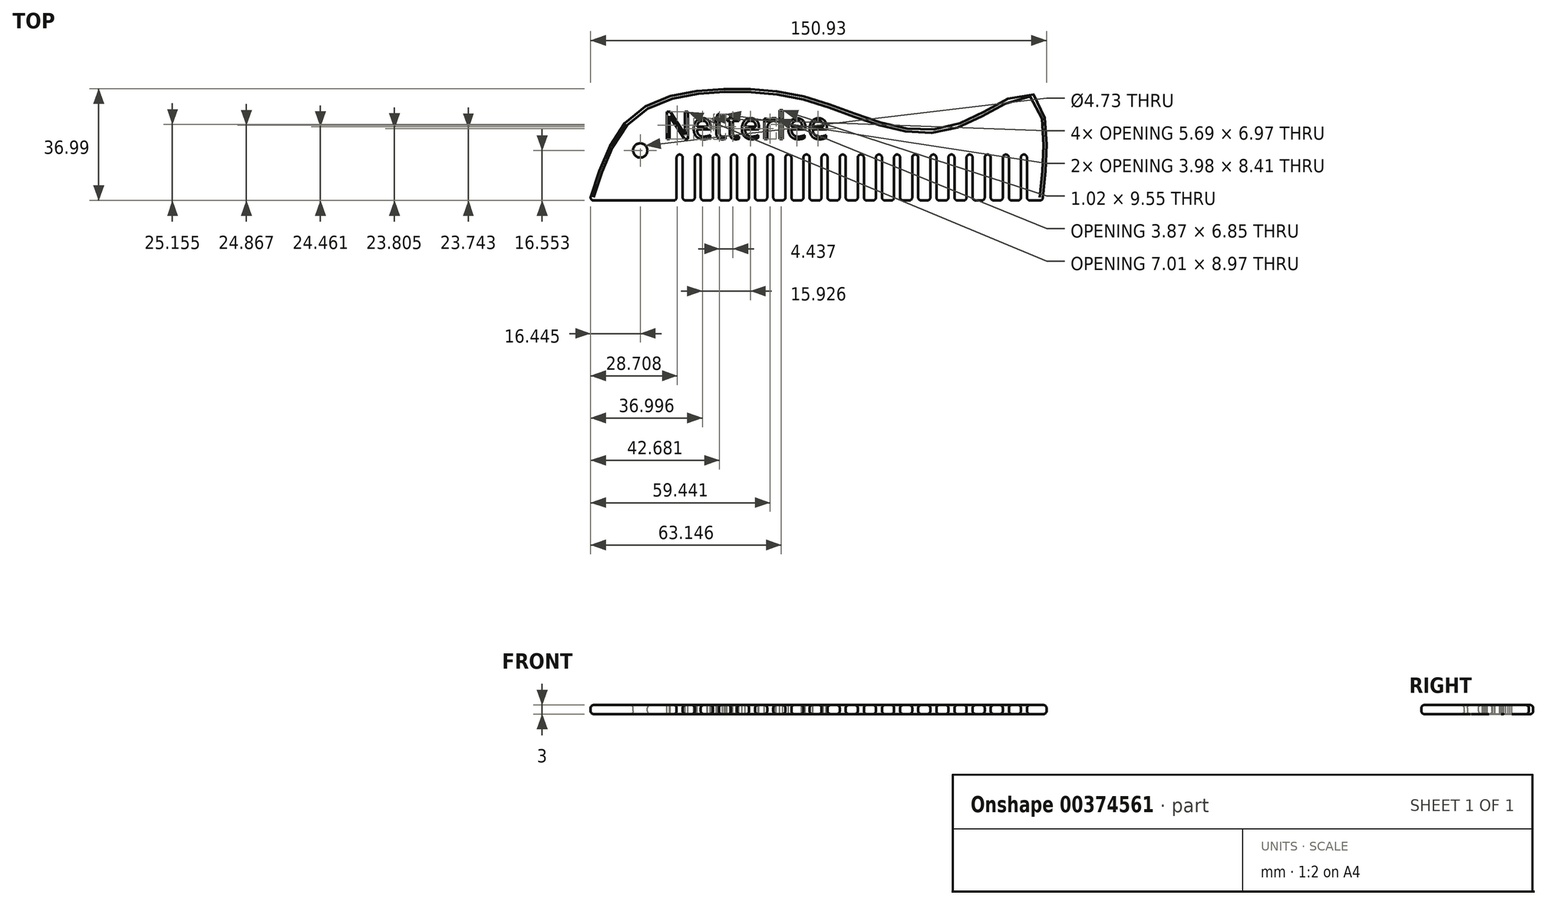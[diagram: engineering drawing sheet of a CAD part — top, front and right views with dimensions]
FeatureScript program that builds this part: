
annotation { "Feature Type Name" : "Feature", "Feature Type Description" : "" }
export const myFeature = defineFeature(function(context is Context, id is Id, definition is map)
    precondition{}
    {
        {
            var Q0;
            Q0=qCreatedBy(makeId("Top.planeOp"),FACE);
            var sketch = newSketch(context, id + "F0", { "sketchPlane" : qUnion([Q0])});
            skFitSpline(sketch, "E0", {"points": [v(-85.57, 36.82) * mm, v(-71.04, 65.23) * mm, v(-42.5, 73.69) * mm, v(-14.03, 71.1) * mm, v(9.11, 63.18) * mm, v(36.67, 62.2) * mm, v(61.65, 71.82) * mm, v(64.09, 33.9) * mm], "startDerivative": vector(69.4, 223.94) * mm, "endDerivative": vector(-31.57, -256.3) * mm});
            skLineSegment(sketch, "E1", {"start": v(-85.57, 36.82) * mm, "end": v(64.43, 36.82) * mm});
            skSolve(sketch);
        }
        {
            var Q0;
            {var subQ0=sQuery(id+"F0.wireOp",EDGE,"E1");Q0=makeQuery(id+"F0.imprint","IMPRINT",FACE,{"disambiguationData":[TD([[makeQuery(id+"F0.imprint","IMPRINT",EDGE,{"derivedFrom":subQ0}),1.0]])]});}
            extrude(context, id + "F1", {"entities" : qUnion([Q0]), "depth" : 3 * mm});
        }
        {
            var Q0;
            Q0=makeQuery(id+"F1.opExtrude","CAP_FACE",FACE,{"disambiguationData":[OSD([sQuery(id+"F0.wireOp",EDGE,"E0"),sQuery(id+"F0.wireOp",EDGE,"E1")])],"isStart":false});
            var sketch = newSketch(context, id + "F2", { "sketchPlane" : qUnion([Q0])});
            skLineSegment(sketch, "E2.bottom", {"start": v(-56.74, 52.03) * mm, "end": v(-54.74, 52.03) * mm});
            skLineSegment(sketch, "E2.top", {"start": v(-56.74, 30.03) * mm, "end": v(-54.74, 30.03) * mm});
            skLineSegment(sketch, "E2.left", {"start": v(-56.74, 52.03) * mm, "end": v(-56.74, 30.03) * mm});
            skLineSegment(sketch, "E2.right", {"start": v(-54.74, 52.03) * mm, "end": v(-54.74, 30.03) * mm});
            skLineSegment(sketch, "E3.1.0.0", {"start": v(-50.74, 52.03) * mm, "end": v(-50.74, 30.03) * mm});
            skLineSegment(sketch, "E3.1.0.1", {"start": v(-50.74, 52.03) * mm, "end": v(-48.74, 52.03) * mm});
            skLineSegment(sketch, "E3.1.0.2", {"start": v(-48.74, 52.03) * mm, "end": v(-48.74, 30.03) * mm});
            skLineSegment(sketch, "E3.1.0.3", {"start": v(-50.74, 30.03) * mm, "end": v(-48.74, 30.03) * mm});
            skLineSegment(sketch, "E3.2.0.0", {"start": v(-44.74, 52.03) * mm, "end": v(-44.74, 30.03) * mm});
            skLineSegment(sketch, "E3.2.0.1", {"start": v(-44.74, 52.03) * mm, "end": v(-42.74, 52.03) * mm});
            skLineSegment(sketch, "E3.2.0.2", {"start": v(-42.74, 52.03) * mm, "end": v(-42.74, 30.03) * mm});
            skLineSegment(sketch, "E3.2.0.3", {"start": v(-44.74, 30.03) * mm, "end": v(-42.74, 30.03) * mm});
            skLineSegment(sketch, "E3.3.0.0", {"start": v(-38.74, 52.03) * mm, "end": v(-38.74, 30.03) * mm});
            skLineSegment(sketch, "E3.3.0.1", {"start": v(-38.74, 52.03) * mm, "end": v(-36.74, 52.03) * mm});
            skLineSegment(sketch, "E3.3.0.2", {"start": v(-36.74, 52.03) * mm, "end": v(-36.74, 30.03) * mm});
            skLineSegment(sketch, "E3.3.0.3", {"start": v(-38.74, 30.03) * mm, "end": v(-36.74, 30.03) * mm});
            skLineSegment(sketch, "E3.4.0.0", {"start": v(-32.74, 52.03) * mm, "end": v(-32.74, 30.03) * mm});
            skLineSegment(sketch, "E3.4.0.1", {"start": v(-32.74, 52.03) * mm, "end": v(-30.74, 52.03) * mm});
            skLineSegment(sketch, "E3.4.0.2", {"start": v(-30.74, 52.03) * mm, "end": v(-30.74, 30.03) * mm});
            skLineSegment(sketch, "E3.4.0.3", {"start": v(-32.74, 30.03) * mm, "end": v(-30.74, 30.03) * mm});
            skLineSegment(sketch, "E3.5.0.0", {"start": v(-26.74, 52.03) * mm, "end": v(-26.74, 30.03) * mm});
            skLineSegment(sketch, "E3.5.0.1", {"start": v(-26.74, 52.03) * mm, "end": v(-24.74, 52.03) * mm});
            skLineSegment(sketch, "E3.5.0.2", {"start": v(-24.74, 52.03) * mm, "end": v(-24.74, 30.03) * mm});
            skLineSegment(sketch, "E3.5.0.3", {"start": v(-26.74, 30.03) * mm, "end": v(-24.74, 30.03) * mm});
            skLineSegment(sketch, "E3.6.0.0", {"start": v(-20.74, 52.03) * mm, "end": v(-20.74, 30.03) * mm});
            skLineSegment(sketch, "E3.6.0.1", {"start": v(-20.74, 52.03) * mm, "end": v(-18.74, 52.03) * mm});
            skLineSegment(sketch, "E3.6.0.2", {"start": v(-18.74, 52.03) * mm, "end": v(-18.74, 30.03) * mm});
            skLineSegment(sketch, "E3.6.0.3", {"start": v(-20.74, 30.03) * mm, "end": v(-18.74, 30.03) * mm});
            skLineSegment(sketch, "E3.7.0.0", {"start": v(-14.74, 52.03) * mm, "end": v(-14.74, 30.03) * mm});
            skLineSegment(sketch, "E3.7.0.1", {"start": v(-14.74, 52.03) * mm, "end": v(-12.74, 52.03) * mm});
            skLineSegment(sketch, "E3.7.0.2", {"start": v(-12.74, 52.03) * mm, "end": v(-12.74, 30.03) * mm});
            skLineSegment(sketch, "E3.7.0.3", {"start": v(-14.74, 30.03) * mm, "end": v(-12.74, 30.03) * mm});
            skLineSegment(sketch, "E3.8.0.0", {"start": v(-8.74, 52.03) * mm, "end": v(-8.74, 30.03) * mm});
            skLineSegment(sketch, "E3.8.0.1", {"start": v(-8.74, 52.03) * mm, "end": v(-6.74, 52.03) * mm});
            skLineSegment(sketch, "E3.8.0.2", {"start": v(-6.74, 52.03) * mm, "end": v(-6.74, 30.03) * mm});
            skLineSegment(sketch, "E3.8.0.3", {"start": v(-8.74, 30.03) * mm, "end": v(-6.74, 30.03) * mm});
            skLineSegment(sketch, "E3.9.0.0", {"start": v(-2.74, 52.03) * mm, "end": v(-2.74, 30.03) * mm});
            skLineSegment(sketch, "E3.9.0.1", {"start": v(-2.74, 52.03) * mm, "end": v(-0.74, 52.03) * mm});
            skLineSegment(sketch, "E3.9.0.2", {"start": v(-0.74, 52.03) * mm, "end": v(-0.74, 30.03) * mm});
            skLineSegment(sketch, "E3.9.0.3", {"start": v(-2.74, 30.03) * mm, "end": v(-0.74, 30.03) * mm});
            skLineSegment(sketch, "E3.10.0.0", {"start": v(3.26, 52.03) * mm, "end": v(3.26, 30.03) * mm});
            skLineSegment(sketch, "E3.10.0.1", {"start": v(3.26, 52.03) * mm, "end": v(5.26, 52.03) * mm});
            skLineSegment(sketch, "E3.10.0.2", {"start": v(5.26, 52.03) * mm, "end": v(5.26, 30.03) * mm});
            skLineSegment(sketch, "E3.10.0.3", {"start": v(3.26, 30.03) * mm, "end": v(5.26, 30.03) * mm});
            skLineSegment(sketch, "E3.11.0.0", {"start": v(9.26, 52.03) * mm, "end": v(9.26, 30.03) * mm});
            skLineSegment(sketch, "E3.11.0.1", {"start": v(9.26, 52.03) * mm, "end": v(11.26, 52.03) * mm});
            skLineSegment(sketch, "E3.11.0.2", {"start": v(11.26, 52.03) * mm, "end": v(11.26, 30.03) * mm});
            skLineSegment(sketch, "E3.11.0.3", {"start": v(9.26, 30.03) * mm, "end": v(11.26, 30.03) * mm});
            skLineSegment(sketch, "E3.12.0.0", {"start": v(15.26, 52.03) * mm, "end": v(15.26, 30.03) * mm});
            skLineSegment(sketch, "E3.12.0.1", {"start": v(15.26, 52.03) * mm, "end": v(17.26, 52.03) * mm});
            skLineSegment(sketch, "E3.12.0.2", {"start": v(17.26, 52.03) * mm, "end": v(17.26, 30.03) * mm});
            skLineSegment(sketch, "E3.12.0.3", {"start": v(15.26, 30.03) * mm, "end": v(17.26, 30.03) * mm});
            skLineSegment(sketch, "E3.13.0.0", {"start": v(21.26, 52.03) * mm, "end": v(21.26, 30.03) * mm});
            skLineSegment(sketch, "E3.13.0.1", {"start": v(21.26, 52.03) * mm, "end": v(23.26, 52.03) * mm});
            skLineSegment(sketch, "E3.13.0.2", {"start": v(23.26, 52.03) * mm, "end": v(23.26, 30.03) * mm});
            skLineSegment(sketch, "E3.13.0.3", {"start": v(21.26, 30.03) * mm, "end": v(23.26, 30.03) * mm});
            skLineSegment(sketch, "E3.14.0.0", {"start": v(27.26, 52.03) * mm, "end": v(27.26, 30.03) * mm});
            skLineSegment(sketch, "E3.14.0.1", {"start": v(27.26, 52.03) * mm, "end": v(29.26, 52.03) * mm});
            skLineSegment(sketch, "E3.14.0.2", {"start": v(29.26, 52.03) * mm, "end": v(29.26, 30.03) * mm});
            skLineSegment(sketch, "E3.14.0.3", {"start": v(27.26, 30.03) * mm, "end": v(29.26, 30.03) * mm});
            skLineSegment(sketch, "E3.direction1", {"start": v(-54.74, 30.03) * mm, "end": v(-48.74, 30.03) * mm, "construction": true});
            skLineSegment(sketch, "E4.0.15.0", {"start": v(33.26, 52.03) * mm, "end": v(33.26, 30.03) * mm});
            skLineSegment(sketch, "E4.3.15.0", {"start": v(33.26, 52.03) * mm, "end": v(35.26, 52.03) * mm});
            skLineSegment(sketch, "E4.6.15.0", {"start": v(35.26, 52.03) * mm, "end": v(35.26, 30.03) * mm});
            skLineSegment(sketch, "E4.9.15.0", {"start": v(33.26, 30.03) * mm, "end": v(35.26, 30.03) * mm});
            skLineSegment(sketch, "E4.0.16.0", {"start": v(39.26, 52.03) * mm, "end": v(39.26, 30.03) * mm});
            skLineSegment(sketch, "E4.3.16.0", {"start": v(39.26, 52.03) * mm, "end": v(41.26, 52.03) * mm});
            skLineSegment(sketch, "E4.6.16.0", {"start": v(41.26, 52.03) * mm, "end": v(41.26, 30.03) * mm});
            skLineSegment(sketch, "E4.9.16.0", {"start": v(39.26, 30.03) * mm, "end": v(41.26, 30.03) * mm});
            skLineSegment(sketch, "E4.0.17.0", {"start": v(45.26, 52.03) * mm, "end": v(45.26, 30.03) * mm});
            skLineSegment(sketch, "E4.3.17.0", {"start": v(45.26, 52.03) * mm, "end": v(47.26, 52.03) * mm});
            skLineSegment(sketch, "E4.6.17.0", {"start": v(47.26, 52.03) * mm, "end": v(47.26, 30.03) * mm});
            skLineSegment(sketch, "E4.9.17.0", {"start": v(45.26, 30.03) * mm, "end": v(47.26, 30.03) * mm});
            skLineSegment(sketch, "E5.0.18.0", {"start": v(51.26, 52.03) * mm, "end": v(51.26, 30.03) * mm});
            skLineSegment(sketch, "E5.3.18.0", {"start": v(51.26, 52.03) * mm, "end": v(53.26, 52.03) * mm});
            skLineSegment(sketch, "E5.6.18.0", {"start": v(53.26, 52.03) * mm, "end": v(53.26, 30.03) * mm});
            skLineSegment(sketch, "E5.9.18.0", {"start": v(51.26, 30.03) * mm, "end": v(53.26, 30.03) * mm});
            skLineSegment(sketch, "E5.0.19.0", {"start": v(57.26, 52.03) * mm, "end": v(57.26, 30.03) * mm});
            skLineSegment(sketch, "E5.3.19.0", {"start": v(57.26, 52.03) * mm, "end": v(59.26, 52.03) * mm});
            skLineSegment(sketch, "E5.6.19.0", {"start": v(59.26, 52.03) * mm, "end": v(59.26, 30.03) * mm});
            skLineSegment(sketch, "E5.9.19.0", {"start": v(57.26, 30.03) * mm, "end": v(59.26, 30.03) * mm});
            skCircle(sketch, "E6", {"center": v(-70.33, 52.78) * mm, "radius": 2.54 * mm});
            skSolve(sketch);
        }
        {
            var Q0;
            {var subQ0=sQuery(id+"F2.wireOp",EDGE,"E2.bottom");Q0=makeQuery(id+"F2.imprint","IMPRINT",FACE,{"disambiguationData":[TD([[makeQuery(id+"F2.imprint","IMPRINT",EDGE,{"derivedFrom":subQ0}),-1.0]])]});}
            var Q1;
            {var subQ0=sQuery(id+"F2.wireOp",EDGE,"E3.1.0.1");Q1=makeQuery(id+"F2.imprint","IMPRINT",FACE,{"disambiguationData":[TD([[makeQuery(id+"F2.imprint","IMPRINT",EDGE,{"derivedFrom":subQ0}),-1.0]])]});}
            var Q2;
            {var subQ0=sQuery(id+"F2.wireOp",EDGE,"E3.2.0.1");Q2=makeQuery(id+"F2.imprint","IMPRINT",FACE,{"disambiguationData":[TD([[makeQuery(id+"F2.imprint","IMPRINT",EDGE,{"derivedFrom":subQ0}),-1.0]])]});}
            var Q3;
            {var subQ0=sQuery(id+"F2.wireOp",EDGE,"E3.3.0.1");Q3=makeQuery(id+"F2.imprint","IMPRINT",FACE,{"disambiguationData":[TD([[makeQuery(id+"F2.imprint","IMPRINT",EDGE,{"derivedFrom":subQ0}),-1.0]])]});}
            var Q4;
            {var subQ0=sQuery(id+"F2.wireOp",EDGE,"E3.4.0.1");Q4=makeQuery(id+"F2.imprint","IMPRINT",FACE,{"disambiguationData":[TD([[makeQuery(id+"F2.imprint","IMPRINT",EDGE,{"derivedFrom":subQ0}),-1.0]])]});}
            var Q5;
            {var subQ0=sQuery(id+"F2.wireOp",EDGE,"E3.5.0.1");Q5=makeQuery(id+"F2.imprint","IMPRINT",FACE,{"disambiguationData":[TD([[makeQuery(id+"F2.imprint","IMPRINT",EDGE,{"derivedFrom":subQ0}),-1.0]])]});}
            var Q6;
            {var subQ0=sQuery(id+"F2.wireOp",EDGE,"E3.6.0.1");Q6=makeQuery(id+"F2.imprint","IMPRINT",FACE,{"disambiguationData":[TD([[makeQuery(id+"F2.imprint","IMPRINT",EDGE,{"derivedFrom":subQ0}),-1.0]])]});}
            var Q7;
            {var subQ0=sQuery(id+"F2.wireOp",EDGE,"E3.7.0.1");Q7=makeQuery(id+"F2.imprint","IMPRINT",FACE,{"disambiguationData":[TD([[makeQuery(id+"F2.imprint","IMPRINT",EDGE,{"derivedFrom":subQ0}),-1.0]])]});}
            var Q8;
            {var subQ0=sQuery(id+"F2.wireOp",EDGE,"E3.8.0.1");Q8=makeQuery(id+"F2.imprint","IMPRINT",FACE,{"disambiguationData":[TD([[makeQuery(id+"F2.imprint","IMPRINT",EDGE,{"derivedFrom":subQ0}),-1.0]])]});}
            var Q9;
            {var subQ0=sQuery(id+"F2.wireOp",EDGE,"E3.9.0.1");Q9=makeQuery(id+"F2.imprint","IMPRINT",FACE,{"disambiguationData":[TD([[makeQuery(id+"F2.imprint","IMPRINT",EDGE,{"derivedFrom":subQ0}),-1.0]])]});}
            var Q10;
            {var subQ0=sQuery(id+"F2.wireOp",EDGE,"E3.10.0.1");Q10=makeQuery(id+"F2.imprint","IMPRINT",FACE,{"disambiguationData":[TD([[makeQuery(id+"F2.imprint","IMPRINT",EDGE,{"derivedFrom":subQ0}),-1.0]])]});}
            var Q11;
            {var subQ0=sQuery(id+"F2.wireOp",EDGE,"E3.11.0.1");Q11=makeQuery(id+"F2.imprint","IMPRINT",FACE,{"disambiguationData":[TD([[makeQuery(id+"F2.imprint","IMPRINT",EDGE,{"derivedFrom":subQ0}),-1.0]])]});}
            var Q12;
            {var subQ0=sQuery(id+"F2.wireOp",EDGE,"E3.12.0.1");Q12=makeQuery(id+"F2.imprint","IMPRINT",FACE,{"disambiguationData":[TD([[makeQuery(id+"F2.imprint","IMPRINT",EDGE,{"derivedFrom":subQ0}),-1.0]])]});}
            var Q13;
            {var subQ0=sQuery(id+"F2.wireOp",EDGE,"E3.13.0.1");Q13=makeQuery(id+"F2.imprint","IMPRINT",FACE,{"disambiguationData":[TD([[makeQuery(id+"F2.imprint","IMPRINT",EDGE,{"derivedFrom":subQ0}),-1.0]])]});}
            var Q14;
            {var subQ0=sQuery(id+"F2.wireOp",EDGE,"E3.14.0.1");Q14=makeQuery(id+"F2.imprint","IMPRINT",FACE,{"disambiguationData":[TD([[makeQuery(id+"F2.imprint","IMPRINT",EDGE,{"derivedFrom":subQ0}),-1.0]])]});}
            var Q15;
            {var subQ0=sQuery(id+"F2.wireOp",EDGE,"E4.3.15.0");Q15=makeQuery(id+"F2.imprint","IMPRINT",FACE,{"disambiguationData":[TD([[makeQuery(id+"F2.imprint","IMPRINT",EDGE,{"derivedFrom":subQ0}),-1.0]])]});}
            var Q16;
            {var subQ0=sQuery(id+"F2.wireOp",EDGE,"E4.3.16.0");Q16=makeQuery(id+"F2.imprint","IMPRINT",FACE,{"disambiguationData":[TD([[makeQuery(id+"F2.imprint","IMPRINT",EDGE,{"derivedFrom":subQ0}),-1.0]])]});}
            var Q17;
            {var subQ0=sQuery(id+"F2.wireOp",EDGE,"E4.3.17.0");Q17=makeQuery(id+"F2.imprint","IMPRINT",FACE,{"disambiguationData":[TD([[makeQuery(id+"F2.imprint","IMPRINT",EDGE,{"derivedFrom":subQ0}),-1.0]])]});}
            var Q18;
            {var subQ0=sQuery(id+"F2.wireOp",EDGE,"E5.3.18.0");Q18=makeQuery(id+"F2.imprint","IMPRINT",FACE,{"disambiguationData":[TD([[makeQuery(id+"F2.imprint","IMPRINT",EDGE,{"derivedFrom":subQ0}),-1.0]])]});}
            var Q19;
            {var subQ0=sQuery(id+"F2.wireOp",EDGE,"E5.3.19.0");Q19=makeQuery(id+"F2.imprint","IMPRINT",FACE,{"disambiguationData":[TD([[makeQuery(id+"F2.imprint","IMPRINT",EDGE,{"derivedFrom":subQ0}),-1.0]])]});}
            extrude(context, id + "F3", {"entities" : qUnion([Q0, Q1, Q2, Q3, Q4, Q5, Q6, Q7, Q8, Q9, Q10, Q11, Q12, Q13, Q14, Q15, Q16, Q17, Q18, Q19]), "operationType" : NewBodyOperationType.REMOVE, "oppositeDirection" : true, "depth" : 5 * mm});
        }
        {
            var Q0;
            Q0=makeQuery(id+"F3.boolean.opBoolean","COPY",FACE,{"derivedFrom":makeQuery(id+"F3.opExtrude","SWEPT_FACE",FACE,{"disambiguationData":[OSD([sQuery(id+"F2.wireOp",EDGE,"E3.5.0.0")])]})});
            var Q1;
            Q1=makeQuery(id+"F1.opExtrude","CAP_EDGE",EDGE,{"disambiguationData":[OSD([sQuery(id+"F0.wireOp",EDGE,"E0")])],"isStart":false});
            var Q2;
            Q2=makeQuery(id+"F1.opExtrude","CAP_EDGE",EDGE,{"disambiguationData":[OSD([sQuery(id+"F0.wireOp",EDGE,"E0")])],"isStart":true});
            var Q3;
            Q3=makeQuery(id+"F1.opExtrude","SWEPT_FACE",FACE,{"disambiguationData":[OSD([sQuery(id+"F0.wireOp",EDGE,"E0")])]});
            var Q4;
            Q4=makeQuery(id+"F3.boolean.opBoolean","COPY",FACE,{"derivedFrom":makeQuery(id+"F3.opExtrude","SWEPT_FACE",FACE,{"disambiguationData":[OSD([sQuery(id+"F2.wireOp",EDGE,"E3.4.0.2")])]})});
            var Q5;
            Q5=makeQuery(id+"F3.boolean.opBoolean","COPY",FACE,{"derivedFrom":makeQuery(id+"F3.opExtrude","SWEPT_FACE",FACE,{"disambiguationData":[OSD([sQuery(id+"F2.wireOp",EDGE,"E2.left")])]})});
            var Q6;
            Q6=makeQuery(id+"F3.boolean.opBoolean","COPY",FACE,{"derivedFrom":makeQuery(id+"F3.opExtrude","SWEPT_FACE",FACE,{"disambiguationData":[OSD([sQuery(id+"F2.wireOp",EDGE,"E2.right")])]})});
            var Q7;
            Q7=makeQuery(id+"F3.boolean.opBoolean","COPY",FACE,{"derivedFrom":makeQuery(id+"F3.opExtrude","SWEPT_FACE",FACE,{"disambiguationData":[OSD([sQuery(id+"F2.wireOp",EDGE,"E3.1.0.0")])]})});
            var Q8;
            Q8=makeQuery(id+"F3.boolean.opBoolean","COPY",FACE,{"derivedFrom":makeQuery(id+"F3.opExtrude","SWEPT_FACE",FACE,{"disambiguationData":[OSD([sQuery(id+"F2.wireOp",EDGE,"E3.1.0.2")])]})});
            var Q9;
            Q9=makeQuery(id+"F3.boolean.opBoolean","COPY",FACE,{"derivedFrom":makeQuery(id+"F3.opExtrude","SWEPT_FACE",FACE,{"disambiguationData":[OSD([sQuery(id+"F2.wireOp",EDGE,"E3.2.0.0")])]})});
            var Q10;
            Q10=makeQuery(id+"F3.boolean.opBoolean","COPY",FACE,{"derivedFrom":makeQuery(id+"F3.opExtrude","SWEPT_FACE",FACE,{"disambiguationData":[OSD([sQuery(id+"F2.wireOp",EDGE,"E3.2.0.2")])]})});
            var Q11;
            Q11=makeQuery(id+"F3.boolean.opBoolean","COPY",FACE,{"derivedFrom":makeQuery(id+"F3.opExtrude","SWEPT_FACE",FACE,{"disambiguationData":[OSD([sQuery(id+"F2.wireOp",EDGE,"E3.3.0.0")])]})});
            var Q12;
            Q12=makeQuery(id+"F3.boolean.opBoolean","COPY",FACE,{"derivedFrom":makeQuery(id+"F3.opExtrude","SWEPT_FACE",FACE,{"disambiguationData":[OSD([sQuery(id+"F2.wireOp",EDGE,"E3.3.0.2")])]})});
            var Q13;
            Q13=makeQuery(id+"F3.boolean.opBoolean","COPY",FACE,{"derivedFrom":makeQuery(id+"F3.opExtrude","SWEPT_FACE",FACE,{"disambiguationData":[OSD([sQuery(id+"F2.wireOp",EDGE,"E3.4.0.0")])]})});
            var Q14;
            Q14=makeQuery(id+"F3.boolean.opBoolean","COPY",FACE,{"derivedFrom":makeQuery(id+"F3.opExtrude","SWEPT_FACE",FACE,{"disambiguationData":[OSD([sQuery(id+"F2.wireOp",EDGE,"E4.6.15.0")])]})});
            var Q15;
            {var subQ1=sQuery(id+"F0.wireOp",EDGE,"E1");Q15=makeQuery(id+"F3.boolean.opBoolean","SPLIT",FACE,{"disambiguationData":[TD([makeQuery(id+"F3.opExtrude","SWEPT_FACE",FACE,{"disambiguationData":[OSD([sQuery(id+"F2.wireOp",EDGE,"E5.6.19.0")])]})])],"derivedFrom":makeQuery(id+"F1.opExtrude","SWEPT_FACE",FACE,{"disambiguationData":[OSD([subQ1])]})});}
            var Q16;
            Q16=makeQuery(id+"F3.boolean.opBoolean","COPY",EDGE,{"derivedFrom":makeQuery(id+"F3.opExtrude","CAP_EDGE",EDGE,{"disambiguationData":[OSD([sQuery(id+"F2.wireOp",EDGE,"E3.9.0.2")])],"isStart":true})});
            var Q17;
            Q17=makeQuery(id+"F3.boolean.opBoolean","COPY",EDGE,{"derivedFrom":makeQuery(id+"F3.opExtrude","CAP_EDGE",EDGE,{"disambiguationData":[OSD([sQuery(id+"F2.wireOp",EDGE,"E4.0.15.0")])],"isStart":true})});
            var Q18;
            Q18=makeQuery(id+"F3.boolean.opBoolean","COPY",FACE,{"derivedFrom":makeQuery(id+"F3.opExtrude","SWEPT_FACE",FACE,{"disambiguationData":[OSD([sQuery(id+"F2.wireOp",EDGE,"E3.9.0.2")])]})});
            var Q19;
            Q19=makeQuery(id+"F3.boolean.opBoolean","COPY",FACE,{"derivedFrom":makeQuery(id+"F3.opExtrude","SWEPT_FACE",FACE,{"disambiguationData":[OSD([sQuery(id+"F2.wireOp",EDGE,"E4.0.15.0")])]})});
            var Q20;
            Q20=makeQuery(id+"F1.opExtrude","CAP_FACE",FACE,{"disambiguationData":[OSD([sQuery(id+"F0.wireOp",EDGE,"E0"),sQuery(id+"F0.wireOp",EDGE,"E1")])],"isStart":false});
            var Q21;
            Q21=makeQuery(id+"F3.boolean.opBoolean","COPY",EDGE,{"derivedFrom":makeQuery(id+"F3.opExtrude","CAP_EDGE",EDGE,{"disambiguationData":[OSD([sQuery(id+"F2.wireOp",EDGE,"E3.4.0.2")])],"isStart":true})});
            var Q22;
            Q22=makeQuery(id+"F3.boolean.opBoolean","COPY",EDGE,{"derivedFrom":makeQuery(id+"F3.opExtrude","CAP_EDGE",EDGE,{"disambiguationData":[OSD([sQuery(id+"F2.wireOp",EDGE,"E3.10.0.0")])],"isStart":true})});
            var Q23;
            Q23=makeQuery(id+"F3.boolean.opBoolean","COPY",FACE,{"derivedFrom":makeQuery(id+"F3.opExtrude","SWEPT_FACE",FACE,{"disambiguationData":[OSD([sQuery(id+"F2.wireOp",EDGE,"E3.10.0.0")])]})});
            var Q24;
            {var subQ1=sQuery(id+"F0.wireOp",EDGE,"E1");Q24=makeQuery(id+"F3.boolean.opBoolean","SPLIT",FACE,{"disambiguationData":[TD([makeQuery(id+"F3.opExtrude","SWEPT_FACE",FACE,{"disambiguationData":[OSD([sQuery(id+"F2.wireOp",EDGE,"E2.left")])]})])],"derivedFrom":makeQuery(id+"F1.opExtrude","SWEPT_FACE",FACE,{"disambiguationData":[OSD([subQ1])]})});}
            var Q25;
            Q25=makeQuery(id+"F3.boolean.opBoolean","COPY",EDGE,{"derivedFrom":makeQuery(id+"F3.opExtrude","CAP_EDGE",EDGE,{"disambiguationData":[OSD([sQuery(id+"F2.wireOp",EDGE,"E3.5.0.0")])],"isStart":true})});
            var Q26;
            Q26=makeQuery(id+"F3.boolean.opBoolean","COPY",EDGE,{"derivedFrom":makeQuery(id+"F3.opExtrude","CAP_EDGE",EDGE,{"disambiguationData":[OSD([sQuery(id+"F2.wireOp",EDGE,"E4.6.15.0")])],"isStart":true})});
            var Q27;
            Q27=makeQuery(id+"F3.boolean.opBoolean","COPY",EDGE,{"derivedFrom":makeQuery(id+"F3.opExtrude","CAP_EDGE",EDGE,{"disambiguationData":[OSD([sQuery(id+"F2.wireOp",EDGE,"E3.10.0.2")])],"isStart":true})});
            var Q28;
            Q28=makeQuery(id+"F3.boolean.opBoolean","COPY",EDGE,{"derivedFrom":makeQuery(id+"F3.opExtrude","CAP_EDGE",EDGE,{"disambiguationData":[OSD([sQuery(id+"F2.wireOp",EDGE,"E4.0.16.0")])],"isStart":true})});
            var Q29;
            Q29=makeQuery(id+"F3.boolean.opBoolean","COPY",FACE,{"derivedFrom":makeQuery(id+"F3.opExtrude","SWEPT_FACE",FACE,{"disambiguationData":[OSD([sQuery(id+"F2.wireOp",EDGE,"E3.10.0.2")])]})});
            var Q30;
            Q30=makeQuery(id+"F3.boolean.opBoolean","COPY",FACE,{"derivedFrom":makeQuery(id+"F3.opExtrude","SWEPT_FACE",FACE,{"disambiguationData":[OSD([sQuery(id+"F2.wireOp",EDGE,"E4.0.16.0")])]})});
            var Q31;
            Q31=makeQuery(id+"F3.boolean.opBoolean","COPY",EDGE,{"derivedFrom":makeQuery(id+"F3.opExtrude","CAP_EDGE",EDGE,{"disambiguationData":[OSD([sQuery(id+"F2.wireOp",EDGE,"E2.left")])],"isStart":true})});
            var Q32;
            Q32=makeQuery(id+"F3.boolean.opBoolean","COPY",EDGE,{"derivedFrom":makeQuery(id+"F3.opExtrude","CAP_EDGE",EDGE,{"disambiguationData":[OSD([sQuery(id+"F2.wireOp",EDGE,"E3.5.0.2")])],"isStart":true})});
            var Q33;
            Q33=makeQuery(id+"F3.boolean.opBoolean","COPY",EDGE,{"derivedFrom":makeQuery(id+"F3.opExtrude","CAP_EDGE",EDGE,{"disambiguationData":[OSD([sQuery(id+"F2.wireOp",EDGE,"E3.11.0.0")])],"isStart":true})});
            var Q34;
            Q34=makeQuery(id+"F3.boolean.opBoolean","COPY",FACE,{"derivedFrom":makeQuery(id+"F3.opExtrude","SWEPT_FACE",FACE,{"disambiguationData":[OSD([sQuery(id+"F2.wireOp",EDGE,"E3.5.0.2")])]})});
            var Q35;
            {var subQ0=sQuery(id+"F0.wireOp",EDGE,"E1");Q35=makeQuery(id+"F3.boolean.opBoolean","SPLIT",FACE,{"disambiguationData":[TD([makeQuery(id+"F3.opExtrude","SWEPT_FACE",FACE,{"disambiguationData":[OSD([sQuery(id+"F2.wireOp",EDGE,"E3.1.0.2")])]})])],"derivedFrom":makeQuery(id+"F1.opExtrude","SWEPT_FACE",FACE,{"disambiguationData":[OSD([subQ0])]})});}
            var Q36;
            Q36=makeQuery(id+"F3.boolean.opBoolean","COPY",EDGE,{"derivedFrom":makeQuery(id+"F3.opExtrude","CAP_EDGE",EDGE,{"disambiguationData":[OSD([sQuery(id+"F2.wireOp",EDGE,"E2.right")])],"isStart":true})});
            var Q37;
            Q37=makeQuery(id+"F3.boolean.opBoolean","COPY",FACE,{"derivedFrom":makeQuery(id+"F3.opExtrude","SWEPT_FACE",FACE,{"disambiguationData":[OSD([sQuery(id+"F2.wireOp",EDGE,"E3.6.0.0")])]})});
            var Q38;
            Q38=makeQuery(id+"F3.boolean.opBoolean","COPY",FACE,{"derivedFrom":makeQuery(id+"F3.opExtrude","SWEPT_FACE",FACE,{"disambiguationData":[OSD([sQuery(id+"F2.wireOp",EDGE,"E4.6.16.0")])]})});
            var Q39;
            Q39=makeQuery(id+"F3.boolean.opBoolean","COPY",EDGE,{"derivedFrom":makeQuery(id+"F3.opExtrude","CAP_EDGE",EDGE,{"disambiguationData":[OSD([sQuery(id+"F2.wireOp",EDGE,"E3.1.0.0")])],"isStart":true})});
            var Q40;
            Q40=makeQuery(id+"F3.boolean.opBoolean","COPY",EDGE,{"derivedFrom":makeQuery(id+"F3.opExtrude","CAP_EDGE",EDGE,{"disambiguationData":[OSD([sQuery(id+"F2.wireOp",EDGE,"E3.11.0.2")])],"isStart":true})});
            var Q41;
            Q41=makeQuery(id+"F3.boolean.opBoolean","COPY",EDGE,{"derivedFrom":makeQuery(id+"F3.opExtrude","CAP_EDGE",EDGE,{"disambiguationData":[OSD([sQuery(id+"F2.wireOp",EDGE,"E4.0.17.0")])],"isStart":true})});
            var Q42;
            Q42=makeQuery(id+"F3.boolean.opBoolean","COPY",FACE,{"derivedFrom":makeQuery(id+"F3.opExtrude","SWEPT_FACE",FACE,{"disambiguationData":[OSD([sQuery(id+"F2.wireOp",EDGE,"E3.11.0.2")])]})});
            var Q43;
            Q43=makeQuery(id+"F3.boolean.opBoolean","COPY",FACE,{"derivedFrom":makeQuery(id+"F3.opExtrude","SWEPT_FACE",FACE,{"disambiguationData":[OSD([sQuery(id+"F2.wireOp",EDGE,"E4.0.17.0")])]})});
            var Q44;
            Q44=makeQuery(id+"F3.boolean.opBoolean","COPY",EDGE,{"derivedFrom":makeQuery(id+"F3.opExtrude","CAP_EDGE",EDGE,{"disambiguationData":[OSD([sQuery(id+"F2.wireOp",EDGE,"E3.12.0.0")])],"isStart":true})});
            var Q45;
            Q45=makeQuery(id+"F3.boolean.opBoolean","COPY",FACE,{"derivedFrom":makeQuery(id+"F3.opExtrude","SWEPT_FACE",FACE,{"disambiguationData":[OSD([sQuery(id+"F2.wireOp",EDGE,"E3.6.0.2")])]})});
            var Q46;
            Q46=makeQuery(id+"F3.boolean.opBoolean","COPY",FACE,{"derivedFrom":makeQuery(id+"F3.opExtrude","SWEPT_FACE",FACE,{"disambiguationData":[OSD([sQuery(id+"F2.wireOp",EDGE,"E3.12.0.0")])]})});
            var Q47;
            Q47=makeQuery(id+"F3.boolean.opBoolean","COPY",EDGE,{"derivedFrom":makeQuery(id+"F3.opExtrude","CAP_EDGE",EDGE,{"disambiguationData":[OSD([sQuery(id+"F2.wireOp",EDGE,"E3.7.0.0")])],"isStart":true})});
            var Q48;
            Q48=makeQuery(id+"F3.boolean.opBoolean","COPY",EDGE,{"derivedFrom":makeQuery(id+"F3.opExtrude","CAP_EDGE",EDGE,{"disambiguationData":[OSD([sQuery(id+"F2.wireOp",EDGE,"E4.6.17.0")])],"isStart":true})});
            var Q49;
            Q49=makeQuery(id+"F3.boolean.opBoolean","COPY",FACE,{"derivedFrom":makeQuery(id+"F3.opExtrude","SWEPT_FACE",FACE,{"disambiguationData":[OSD([sQuery(id+"F2.wireOp",EDGE,"E3.7.0.0")])]})});
            var Q50;
            Q50=makeQuery(id+"F3.boolean.opBoolean","COPY",FACE,{"derivedFrom":makeQuery(id+"F3.opExtrude","SWEPT_FACE",FACE,{"disambiguationData":[OSD([sQuery(id+"F2.wireOp",EDGE,"E4.6.17.0")])]})});
            var Q51;
            Q51=makeQuery(id+"F3.boolean.opBoolean","COPY",EDGE,{"derivedFrom":makeQuery(id+"F3.opExtrude","CAP_EDGE",EDGE,{"disambiguationData":[OSD([sQuery(id+"F2.wireOp",EDGE,"E3.2.0.0")])],"isStart":true})});
            var Q52;
            Q52=makeQuery(id+"F3.boolean.opBoolean","COPY",EDGE,{"derivedFrom":makeQuery(id+"F3.opExtrude","CAP_EDGE",EDGE,{"disambiguationData":[OSD([sQuery(id+"F2.wireOp",EDGE,"E3.12.0.2")])],"isStart":true})});
            var Q53;
            Q53=makeQuery(id+"F3.boolean.opBoolean","COPY",EDGE,{"derivedFrom":makeQuery(id+"F3.opExtrude","CAP_EDGE",EDGE,{"disambiguationData":[OSD([sQuery(id+"F2.wireOp",EDGE,"E5.0.18.0")])],"isStart":true})});
            var Q54;
            Q54=makeQuery(id+"F3.boolean.opBoolean","COPY",FACE,{"derivedFrom":makeQuery(id+"F3.opExtrude","SWEPT_FACE",FACE,{"disambiguationData":[OSD([sQuery(id+"F2.wireOp",EDGE,"E3.12.0.2")])]})});
            var Q55;
            Q55=makeQuery(id+"F3.boolean.opBoolean","COPY",FACE,{"derivedFrom":makeQuery(id+"F3.opExtrude","SWEPT_FACE",FACE,{"disambiguationData":[OSD([sQuery(id+"F2.wireOp",EDGE,"E5.0.18.0")])]})});
            var Q56;
            Q56=makeQuery(id+"F3.boolean.opBoolean","COPY",EDGE,{"derivedFrom":makeQuery(id+"F3.opExtrude","CAP_EDGE",EDGE,{"disambiguationData":[OSD([sQuery(id+"F2.wireOp",EDGE,"E3.7.0.2")])],"isStart":true})});
            var Q57;
            Q57=makeQuery(id+"F3.boolean.opBoolean","COPY",EDGE,{"derivedFrom":makeQuery(id+"F3.opExtrude","CAP_EDGE",EDGE,{"disambiguationData":[OSD([sQuery(id+"F2.wireOp",EDGE,"E3.13.0.0")])],"isStart":true})});
            var Q58;
            Q58=makeQuery(id+"F3.boolean.opBoolean","COPY",FACE,{"derivedFrom":makeQuery(id+"F3.opExtrude","SWEPT_FACE",FACE,{"disambiguationData":[OSD([sQuery(id+"F2.wireOp",EDGE,"E3.7.0.2")])]})});
            var Q59;
            Q59=makeQuery(id+"F3.boolean.opBoolean","COPY",FACE,{"derivedFrom":makeQuery(id+"F3.opExtrude","SWEPT_FACE",FACE,{"disambiguationData":[OSD([sQuery(id+"F2.wireOp",EDGE,"E3.13.0.0")])]})});
            var Q60;
            Q60=makeQuery(id+"F3.boolean.opBoolean","COPY",EDGE,{"derivedFrom":makeQuery(id+"F3.opExtrude","CAP_EDGE",EDGE,{"disambiguationData":[OSD([sQuery(id+"F2.wireOp",EDGE,"E3.2.0.2")])],"isStart":true})});
            var Q61;
            Q61=makeQuery(id+"F3.boolean.opBoolean","COPY",EDGE,{"derivedFrom":makeQuery(id+"F3.opExtrude","CAP_EDGE",EDGE,{"disambiguationData":[OSD([sQuery(id+"F2.wireOp",EDGE,"E3.8.0.0")])],"isStart":true})});
            var Q62;
            {var subQ1=sQuery(id+"F0.wireOp",EDGE,"E1");Q62=makeQuery(id+"F3.boolean.opBoolean","SPLIT",EDGE,{"disambiguationData":[TD([makeQuery(id+"F3.opExtrude","SWEPT_FACE",FACE,{"disambiguationData":[OSD([sQuery(id+"F2.wireOp",EDGE,"E2.left")])]})])],"derivedFrom":makeQuery(id+"F1.opExtrude","CAP_EDGE",EDGE,{"disambiguationData":[OSD([subQ1])],"isStart":true})});}
            var Q63;
            Q63=makeQuery(id+"F3.boolean.opBoolean","COPY",FACE,{"derivedFrom":makeQuery(id+"F3.opExtrude","SWEPT_FACE",FACE,{"disambiguationData":[OSD([sQuery(id+"F2.wireOp",EDGE,"E3.8.0.0")])]})});
            var Q64;
            Q64=makeQuery(id+"F3.boolean.opBoolean","COPY",EDGE,{"derivedFrom":makeQuery(id+"F3.opExtrude","CAP_EDGE",EDGE,{"disambiguationData":[OSD([sQuery(id+"F2.wireOp",EDGE,"E3.3.0.0")])],"isStart":true})});
            var Q65;
            Q65=makeQuery(id+"F3.boolean.opBoolean","COPY",EDGE,{"derivedFrom":makeQuery(id+"F3.opExtrude","CAP_EDGE",EDGE,{"disambiguationData":[OSD([sQuery(id+"F2.wireOp",EDGE,"E3.13.0.2")])],"isStart":true})});
            var Q66;
            Q66=makeQuery(id+"F3.boolean.opBoolean","COPY",EDGE,{"derivedFrom":makeQuery(id+"F3.opExtrude","CAP_EDGE",EDGE,{"disambiguationData":[OSD([sQuery(id+"F2.wireOp",EDGE,"E5.0.19.0")])],"isStart":true})});
            var Q67;
            Q67=makeQuery(id+"F3.boolean.opBoolean","COPY",FACE,{"derivedFrom":makeQuery(id+"F3.opExtrude","SWEPT_FACE",FACE,{"disambiguationData":[OSD([sQuery(id+"F2.wireOp",EDGE,"E3.13.0.2")])]})});
            var Q68;
            Q68=makeQuery(id+"F3.boolean.opBoolean","COPY",FACE,{"derivedFrom":makeQuery(id+"F3.opExtrude","SWEPT_FACE",FACE,{"disambiguationData":[OSD([sQuery(id+"F2.wireOp",EDGE,"E5.0.19.0")])]})});
            var Q69;
            Q69=makeQuery(id+"F3.boolean.opBoolean","COPY",EDGE,{"derivedFrom":makeQuery(id+"F3.opExtrude","CAP_EDGE",EDGE,{"disambiguationData":[OSD([sQuery(id+"F2.wireOp",EDGE,"E3.8.0.2")])],"isStart":true})});
            var Q70;
            Q70=makeQuery(id+"F3.boolean.opBoolean","COPY",EDGE,{"derivedFrom":makeQuery(id+"F3.opExtrude","CAP_EDGE",EDGE,{"disambiguationData":[OSD([sQuery(id+"F2.wireOp",EDGE,"E3.14.0.0")])],"isStart":true})});
            var Q71;
            {var subQ1=sQuery(id+"F0.wireOp",EDGE,"E1");Q71=makeQuery(id+"F3.boolean.opBoolean","SPLIT",EDGE,{"disambiguationData":[TD([makeQuery(id+"F3.opExtrude","SWEPT_FACE",FACE,{"disambiguationData":[OSD([sQuery(id+"F2.wireOp",EDGE,"E2.left")])]})])],"derivedFrom":makeQuery(id+"F1.opExtrude","CAP_EDGE",EDGE,{"disambiguationData":[OSD([subQ1])],"isStart":false})});}
            var Q72;
            Q72=makeQuery(id+"F3.boolean.opBoolean","COPY",FACE,{"derivedFrom":makeQuery(id+"F3.opExtrude","SWEPT_FACE",FACE,{"disambiguationData":[OSD([sQuery(id+"F2.wireOp",EDGE,"E3.14.0.0")])]})});
            var Q73;
            Q73=makeQuery(id+"F3.boolean.opBoolean","COPY",EDGE,{"derivedFrom":makeQuery(id+"F3.opExtrude","CAP_EDGE",EDGE,{"disambiguationData":[OSD([sQuery(id+"F2.wireOp",EDGE,"E3.3.0.2")])],"isStart":true})});
            var Q74;
            Q74=makeQuery(id+"F3.boolean.opBoolean","COPY",EDGE,{"derivedFrom":makeQuery(id+"F3.opExtrude","CAP_EDGE",EDGE,{"disambiguationData":[OSD([sQuery(id+"F2.wireOp",EDGE,"E3.9.0.0")])],"isStart":true})});
            var Q75;
            Q75=makeQuery(id+"F3.boolean.opBoolean","COPY",EDGE,{"derivedFrom":makeQuery(id+"F3.opExtrude","CAP_EDGE",EDGE,{"disambiguationData":[OSD([sQuery(id+"F2.wireOp",EDGE,"E5.6.19.0")])],"isStart":true})});
            var Q76;
            Q76=makeQuery(id+"F3.boolean.opBoolean","COPY",FACE,{"derivedFrom":makeQuery(id+"F3.opExtrude","SWEPT_FACE",FACE,{"disambiguationData":[OSD([sQuery(id+"F2.wireOp",EDGE,"E5.6.19.0")])]})});
            var Q77;
            Q77=makeQuery(id+"F3.boolean.opBoolean","COPY",EDGE,{"derivedFrom":makeQuery(id+"F3.opExtrude","CAP_EDGE",EDGE,{"disambiguationData":[OSD([sQuery(id+"F2.wireOp",EDGE,"E3.4.0.0")])],"isStart":true})});
            var Q78;
            Q78=makeQuery(id+"F3.boolean.opBoolean","COPY",FACE,{"derivedFrom":makeQuery(id+"F3.opExtrude","SWEPT_FACE",FACE,{"disambiguationData":[OSD([sQuery(id+"F2.wireOp",EDGE,"E3.14.0.2")])]})});
            var Q79;
            Q79=makeQuery(id+"F1.opExtrude","CAP_FACE",FACE,{"disambiguationData":[OSD([sQuery(id+"F0.wireOp",EDGE,"E0"),sQuery(id+"F0.wireOp",EDGE,"E1")])],"isStart":true});
            var Q80;
            Q80=makeQuery(id+"F3.boolean.opBoolean","COPY",EDGE,{"derivedFrom":makeQuery(id+"F3.opExtrude","SWEPT_EDGE",EDGE,{"disambiguationData":[OSD([sQuery(id+"F2.wireOp",EDGE,"E3.6.0.1"),sQuery(id+"F2.wireOp",EDGE,"E3.6.0.2")])]})});
            var Q81;
            Q81=makeQuery(id+"F3.boolean.opBoolean","COPY",FACE,{"derivedFrom":makeQuery(id+"F3.opExtrude","SWEPT_FACE",FACE,{"disambiguationData":[OSD([sQuery(id+"F2.wireOp",EDGE,"E3.4.0.1")])]})});
            var Q82;
            {var subQ0=sQuery(id+"F0.wireOp",EDGE,"E1");var subQ1=sQuery(id+"F0.wireOp",EDGE,"E0");Q82=makeQuery(id+"F1.opExtrude","SWEPT_EDGE",EDGE,{"disambiguationData":[OSD([subQ1,subQ0]),TDD([makeQuery(id+"F0.imprint","INTERSECT",VERTEX,{"disambiguationData":[OD(1.0)],"derivedFrom":[subQ1,subQ0]})])]});}
            var Q83;
            {var subQ0=sQuery(id+"F0.wireOp",EDGE,"E1");var subQ1=sQuery(id+"F0.wireOp",EDGE,"E0");Q83=makeQuery(id+"F1.opExtrude","SWEPT_EDGE",EDGE,{"disambiguationData":[OSD([subQ1,subQ0]),TDD([makeQuery(id+"F0.imprint","INTERSECT",VERTEX,{"disambiguationData":[OD(0.0)],"derivedFrom":[subQ1,subQ0]})])]});}
            var Q84;
            Q84=makeQuery(id+"F3.boolean.opBoolean","COPY",EDGE,{"derivedFrom":makeQuery(id+"F3.opExtrude","SWEPT_EDGE",EDGE,{"disambiguationData":[OSD([sQuery(id+"F2.wireOp",EDGE,"E3.7.0.1"),sQuery(id+"F2.wireOp",EDGE,"E3.7.0.2")])]})});
            var Q85;
            Q85=makeQuery(id+"F3.boolean.opBoolean","COPY",FACE,{"derivedFrom":makeQuery(id+"F3.opExtrude","SWEPT_FACE",FACE,{"disambiguationData":[OSD([sQuery(id+"F2.wireOp",EDGE,"E2.bottom")])]})});
            var Q86;
            Q86=makeQuery(id+"F3.boolean.opBoolean","COPY",EDGE,{"derivedFrom":makeQuery(id+"F3.opExtrude","SWEPT_EDGE",EDGE,{"disambiguationData":[OSD([sQuery(id+"F2.wireOp",EDGE,"E2.bottom"),sQuery(id+"F2.wireOp",EDGE,"E2.right")])]})});
            var Q87;
            Q87=makeQuery(id+"F3.boolean.opBoolean","COPY",EDGE,{"derivedFrom":makeQuery(id+"F3.opExtrude","SWEPT_EDGE",EDGE,{"disambiguationData":[OSD([sQuery(id+"F2.wireOp",EDGE,"E3.1.0.1"),sQuery(id+"F2.wireOp",EDGE,"E3.1.0.2")])]})});
            var Q88;
            Q88=makeQuery(id+"F3.boolean.opBoolean","COPY",FACE,{"derivedFrom":makeQuery(id+"F3.opExtrude","SWEPT_FACE",FACE,{"disambiguationData":[OSD([sQuery(id+"F2.wireOp",EDGE,"E3.1.0.1")])]})});
            var Q89;
            Q89=makeQuery(id+"F3.boolean.opBoolean","COPY",EDGE,{"derivedFrom":makeQuery(id+"F3.opExtrude","SWEPT_EDGE",EDGE,{"disambiguationData":[OSD([sQuery(id+"F2.wireOp",EDGE,"E3.2.0.1"),sQuery(id+"F2.wireOp",EDGE,"E3.2.0.2")])]})});
            var Q90;
            Q90=makeQuery(id+"F3.boolean.opBoolean","COPY",EDGE,{"derivedFrom":makeQuery(id+"F3.opExtrude","SWEPT_EDGE",EDGE,{"disambiguationData":[OSD([sQuery(id+"F2.wireOp",EDGE,"E3.3.0.1"),sQuery(id+"F2.wireOp",EDGE,"E3.3.0.2")])]})});
            var Q91;
            Q91=makeQuery(id+"F3.boolean.opBoolean","COPY",FACE,{"derivedFrom":makeQuery(id+"F3.opExtrude","SWEPT_FACE",FACE,{"disambiguationData":[OSD([sQuery(id+"F2.wireOp",EDGE,"E3.2.0.1")])]})});
            var Q92;
            Q92=makeQuery(id+"F3.boolean.opBoolean","COPY",EDGE,{"derivedFrom":makeQuery(id+"F3.opExtrude","SWEPT_EDGE",EDGE,{"disambiguationData":[OSD([sQuery(id+"F2.wireOp",EDGE,"E3.4.0.1"),sQuery(id+"F2.wireOp",EDGE,"E3.4.0.2")])]})});
            var Q93;
            Q93=makeQuery(id+"F3.boolean.opBoolean","COPY",FACE,{"derivedFrom":makeQuery(id+"F3.opExtrude","SWEPT_FACE",FACE,{"disambiguationData":[OSD([sQuery(id+"F2.wireOp",EDGE,"E3.3.0.1")])]})});
            var Q94;
            Q94=makeQuery(id+"F3.boolean.opBoolean","COPY",EDGE,{"derivedFrom":makeQuery(id+"F3.opExtrude","SWEPT_EDGE",EDGE,{"disambiguationData":[OSD([sQuery(id+"F2.wireOp",EDGE,"E3.5.0.1"),sQuery(id+"F2.wireOp",EDGE,"E3.5.0.2")])]})});
            var Q95;
            Q95=makeQuery(id+"F3.boolean.opBoolean","COPY",FACE,{"derivedFrom":makeQuery(id+"F3.opExtrude","SWEPT_FACE",FACE,{"disambiguationData":[OSD([sQuery(id+"F2.wireOp",EDGE,"E3.10.0.1")])]})});
            var Q96;
            {var subQ0=sQuery(id+"F0.wireOp",EDGE,"E1");Q96=makeQuery(id+"F3.boolean.opBoolean","SPLIT",FACE,{"disambiguationData":[TD([makeQuery(id+"F3.opExtrude","SWEPT_FACE",FACE,{"disambiguationData":[OSD([sQuery(id+"F2.wireOp",EDGE,"E4.6.15.0")])]})])],"derivedFrom":makeQuery(id+"F1.opExtrude","SWEPT_FACE",FACE,{"disambiguationData":[OSD([subQ0])]})});}
            var Q97;
            Q97=makeQuery(id+"F3.boolean.opBoolean","INTERSECT",EDGE,{"derivedFrom":[makeQuery(id+"F1.opExtrude","CAP_FACE",FACE,{"disambiguationData":[OSD([sQuery(id+"F0.wireOp",EDGE,"E0"),sQuery(id+"F0.wireOp",EDGE,"E1")])],"isStart":true}),makeQuery(id+"F3.opExtrude","SWEPT_FACE",FACE,{"disambiguationData":[OSD([sQuery(id+"F2.wireOp",EDGE,"E2.left")])]})]});
            var Q98;
            Q98=makeQuery(id+"F3.boolean.opBoolean","INTERSECT",EDGE,{"derivedFrom":[makeQuery(id+"F1.opExtrude","CAP_FACE",FACE,{"disambiguationData":[OSD([sQuery(id+"F0.wireOp",EDGE,"E0"),sQuery(id+"F0.wireOp",EDGE,"E1")])],"isStart":true}),makeQuery(id+"F3.opExtrude","SWEPT_FACE",FACE,{"disambiguationData":[OSD([sQuery(id+"F2.wireOp",EDGE,"E3.5.0.2")])]})]});
            var Q99;
            Q99=makeQuery(id+"F3.boolean.opBoolean","INTERSECT",EDGE,{"derivedFrom":[makeQuery(id+"F1.opExtrude","CAP_FACE",FACE,{"disambiguationData":[OSD([sQuery(id+"F0.wireOp",EDGE,"E0"),sQuery(id+"F0.wireOp",EDGE,"E1")])],"isStart":true}),makeQuery(id+"F3.opExtrude","SWEPT_FACE",FACE,{"disambiguationData":[OSD([sQuery(id+"F2.wireOp",EDGE,"E3.11.0.0")])]})]});
            var Q100;
            {var subQ0=sQuery(id+"F0.wireOp",EDGE,"E1");Q100=makeQuery(id+"F3.boolean.opBoolean","SPLIT",EDGE,{"disambiguationData":[TD([makeQuery(id+"F3.opExtrude","SWEPT_FACE",FACE,{"disambiguationData":[OSD([sQuery(id+"F2.wireOp",EDGE,"E3.1.0.2")])]})])],"derivedFrom":makeQuery(id+"F1.opExtrude","CAP_EDGE",EDGE,{"disambiguationData":[OSD([subQ0])],"isStart":false})});}
            var Q101;
            {var subQ0=sQuery(id+"F0.wireOp",EDGE,"E1");Q101=makeQuery(id+"F3.boolean.opBoolean","SPLIT",EDGE,{"disambiguationData":[TD([makeQuery(id+"F3.opExtrude","SWEPT_FACE",FACE,{"disambiguationData":[OSD([sQuery(id+"F2.wireOp",EDGE,"E4.6.17.0")])]})])],"derivedFrom":makeQuery(id+"F1.opExtrude","CAP_EDGE",EDGE,{"disambiguationData":[OSD([subQ0])],"isStart":false})});}
            var Q102;
            {var subQ0=sQuery(id+"F0.wireOp",EDGE,"E1");Q102=makeQuery(id+"F3.boolean.opBoolean","SPLIT",EDGE,{"disambiguationData":[TD([makeQuery(id+"F3.opExtrude","SWEPT_FACE",FACE,{"disambiguationData":[OSD([sQuery(id+"F2.wireOp",EDGE,"E3.14.0.2")])]})])],"derivedFrom":makeQuery(id+"F1.opExtrude","CAP_EDGE",EDGE,{"disambiguationData":[OSD([subQ0])],"isStart":true})});}
            var Q103;
            {var subQ0=sQuery(id+"F0.wireOp",EDGE,"E1");Q103=makeQuery(id+"F3.boolean.opBoolean","SPLIT",FACE,{"disambiguationData":[TD([makeQuery(id+"F3.opExtrude","SWEPT_FACE",FACE,{"disambiguationData":[OSD([sQuery(id+"F2.wireOp",EDGE,"E3.13.0.2")])]})])],"derivedFrom":makeQuery(id+"F1.opExtrude","SWEPT_FACE",FACE,{"disambiguationData":[OSD([subQ0])]})});}
            var Q104;
            Q104=makeQuery(id+"F3.boolean.opBoolean","INTERSECT",EDGE,{"derivedFrom":[makeQuery(id+"F1.opExtrude","CAP_FACE",FACE,{"disambiguationData":[OSD([sQuery(id+"F0.wireOp",EDGE,"E0"),sQuery(id+"F0.wireOp",EDGE,"E1")])],"isStart":true}),makeQuery(id+"F3.opExtrude","SWEPT_FACE",FACE,{"disambiguationData":[OSD([sQuery(id+"F2.wireOp",EDGE,"E2.right")])]})]});
            var Q105;
            Q105=makeQuery(id+"F3.boolean.opBoolean","INTERSECT",EDGE,{"derivedFrom":[makeQuery(id+"F1.opExtrude","CAP_FACE",FACE,{"disambiguationData":[OSD([sQuery(id+"F0.wireOp",EDGE,"E0"),sQuery(id+"F0.wireOp",EDGE,"E1")])],"isStart":true}),makeQuery(id+"F3.opExtrude","SWEPT_FACE",FACE,{"disambiguationData":[OSD([sQuery(id+"F2.wireOp",EDGE,"E3.6.0.0")])]})]});
            var Q106;
            Q106=makeQuery(id+"F3.boolean.opBoolean","INTERSECT",EDGE,{"derivedFrom":[makeQuery(id+"F1.opExtrude","CAP_FACE",FACE,{"disambiguationData":[OSD([sQuery(id+"F0.wireOp",EDGE,"E0"),sQuery(id+"F0.wireOp",EDGE,"E1")])],"isStart":true}),makeQuery(id+"F3.opExtrude","SWEPT_FACE",FACE,{"disambiguationData":[OSD([sQuery(id+"F2.wireOp",EDGE,"E4.6.16.0")])]})]});
            var Q107;
            {var subQ0=sQuery(id+"F0.wireOp",EDGE,"E1");Q107=makeQuery(id+"F3.boolean.opBoolean","SPLIT",EDGE,{"disambiguationData":[TD([makeQuery(id+"F3.opExtrude","SWEPT_FACE",FACE,{"disambiguationData":[OSD([sQuery(id+"F2.wireOp",EDGE,"E3.2.0.2")])]})])],"derivedFrom":makeQuery(id+"F1.opExtrude","CAP_EDGE",EDGE,{"disambiguationData":[OSD([subQ0])],"isStart":false})});}
            var Q108;
            {var subQ0=sQuery(id+"F0.wireOp",EDGE,"E1");Q108=makeQuery(id+"F3.boolean.opBoolean","SPLIT",EDGE,{"disambiguationData":[TD([makeQuery(id+"F3.opExtrude","SWEPT_FACE",FACE,{"disambiguationData":[OSD([sQuery(id+"F2.wireOp",EDGE,"E5.6.18.0")])]})])],"derivedFrom":makeQuery(id+"F1.opExtrude","CAP_EDGE",EDGE,{"disambiguationData":[OSD([subQ0])],"isStart":false})});}
            var Q109;
            {var subQ0=sQuery(id+"F0.wireOp",EDGE,"E1");Q109=makeQuery(id+"F3.boolean.opBoolean","SPLIT",EDGE,{"disambiguationData":[TD([makeQuery(id+"F3.opExtrude","SWEPT_FACE",FACE,{"disambiguationData":[OSD([sQuery(id+"F2.wireOp",EDGE,"E4.6.15.0")])]})])],"derivedFrom":makeQuery(id+"F1.opExtrude","CAP_EDGE",EDGE,{"disambiguationData":[OSD([subQ0])],"isStart":true})});}
            var Q110;
            Q110=makeQuery(id+"F3.boolean.opBoolean","COPY",FACE,{"derivedFrom":makeQuery(id+"F3.opExtrude","SWEPT_FACE",FACE,{"disambiguationData":[OSD([sQuery(id+"F2.wireOp",EDGE,"E4.3.15.0")])]})});
            var Q111;
            {var subQ0=sQuery(id+"F0.wireOp",EDGE,"E1");Q111=makeQuery(id+"F3.boolean.opBoolean","SPLIT",FACE,{"disambiguationData":[TD([makeQuery(id+"F3.opExtrude","SWEPT_FACE",FACE,{"disambiguationData":[OSD([sQuery(id+"F2.wireOp",EDGE,"E3.14.0.2")])]})])],"derivedFrom":makeQuery(id+"F1.opExtrude","SWEPT_FACE",FACE,{"disambiguationData":[OSD([subQ0])]})});}
            var Q112;
            Q112=makeQuery(id+"F3.boolean.opBoolean","COPY",EDGE,{"derivedFrom":makeQuery(id+"F3.opExtrude","SWEPT_EDGE",EDGE,{"disambiguationData":[OSD([sQuery(id+"F2.wireOp",EDGE,"E4.3.15.0"),sQuery(id+"F2.wireOp",EDGE,"E4.6.15.0")])]})});
            var Q113;
            Q113=makeQuery(id+"F3.boolean.opBoolean","COPY",EDGE,{"derivedFrom":makeQuery(id+"F3.opExtrude","SWEPT_EDGE",EDGE,{"disambiguationData":[OSD([sQuery(id+"F0.wireOp",EDGE,"E1"),sQuery(id+"F2.wireOp",EDGE,"E5.6.19.0")])]})});
            var Q114;
            Q114=makeQuery(id+"F3.boolean.opBoolean","INTERSECT",EDGE,{"derivedFrom":[makeQuery(id+"F1.opExtrude","CAP_FACE",FACE,{"disambiguationData":[OSD([sQuery(id+"F0.wireOp",EDGE,"E0"),sQuery(id+"F0.wireOp",EDGE,"E1")])],"isStart":true}),makeQuery(id+"F3.opExtrude","SWEPT_FACE",FACE,{"disambiguationData":[OSD([sQuery(id+"F2.wireOp",EDGE,"E3.1.0.0")])]})]});
            var Q115;
            Q115=makeQuery(id+"F3.boolean.opBoolean","INTERSECT",EDGE,{"derivedFrom":[makeQuery(id+"F1.opExtrude","CAP_FACE",FACE,{"disambiguationData":[OSD([sQuery(id+"F0.wireOp",EDGE,"E0"),sQuery(id+"F0.wireOp",EDGE,"E1")])],"isStart":true}),makeQuery(id+"F3.opExtrude","SWEPT_FACE",FACE,{"disambiguationData":[OSD([sQuery(id+"F2.wireOp",EDGE,"E3.11.0.2")])]})]});
            var Q116;
            Q116=makeQuery(id+"F3.boolean.opBoolean","INTERSECT",EDGE,{"derivedFrom":[makeQuery(id+"F1.opExtrude","CAP_FACE",FACE,{"disambiguationData":[OSD([sQuery(id+"F0.wireOp",EDGE,"E0"),sQuery(id+"F0.wireOp",EDGE,"E1")])],"isStart":true}),makeQuery(id+"F3.opExtrude","SWEPT_FACE",FACE,{"disambiguationData":[OSD([sQuery(id+"F2.wireOp",EDGE,"E4.0.17.0")])]})]});
            var Q117;
            {var subQ0=sQuery(id+"F0.wireOp",EDGE,"E1");Q117=makeQuery(id+"F3.boolean.opBoolean","SPLIT",EDGE,{"disambiguationData":[TD([makeQuery(id+"F3.opExtrude","SWEPT_FACE",FACE,{"disambiguationData":[OSD([sQuery(id+"F2.wireOp",EDGE,"E3.3.0.2")])]})])],"derivedFrom":makeQuery(id+"F1.opExtrude","CAP_EDGE",EDGE,{"disambiguationData":[OSD([subQ0])],"isStart":false})});}
            var Q118;
            {var subQ0=sQuery(id+"F0.wireOp",EDGE,"E1");Q118=makeQuery(id+"F3.boolean.opBoolean","SPLIT",EDGE,{"disambiguationData":[TD([makeQuery(id+"F3.opExtrude","SWEPT_FACE",FACE,{"disambiguationData":[OSD([sQuery(id+"F2.wireOp",EDGE,"E2.right")])]})])],"derivedFrom":makeQuery(id+"F1.opExtrude","CAP_EDGE",EDGE,{"disambiguationData":[OSD([subQ0])],"isStart":true})});}
            var Q119;
            {var subQ0=sQuery(id+"F0.wireOp",EDGE,"E1");Q119=makeQuery(id+"F3.boolean.opBoolean","SPLIT",EDGE,{"disambiguationData":[TD([makeQuery(id+"F3.opExtrude","SWEPT_FACE",FACE,{"disambiguationData":[OSD([sQuery(id+"F2.wireOp",EDGE,"E4.6.16.0")])]})])],"derivedFrom":makeQuery(id+"F1.opExtrude","CAP_EDGE",EDGE,{"disambiguationData":[OSD([subQ0])],"isStart":true})});}
            var Q120;
            Q120=makeQuery(id+"F3.boolean.opBoolean","INTERSECT",EDGE,{"derivedFrom":[makeQuery(id+"F1.opExtrude","CAP_FACE",FACE,{"disambiguationData":[OSD([sQuery(id+"F0.wireOp",EDGE,"E0"),sQuery(id+"F0.wireOp",EDGE,"E1")])],"isStart":true}),makeQuery(id+"F3.opExtrude","SWEPT_FACE",FACE,{"disambiguationData":[OSD([sQuery(id+"F2.wireOp",EDGE,"E3.6.0.2")])]})]});
            var Q121;
            Q121=makeQuery(id+"F3.boolean.opBoolean","INTERSECT",EDGE,{"derivedFrom":[makeQuery(id+"F1.opExtrude","CAP_FACE",FACE,{"disambiguationData":[OSD([sQuery(id+"F0.wireOp",EDGE,"E0"),sQuery(id+"F0.wireOp",EDGE,"E1")])],"isStart":true}),makeQuery(id+"F3.opExtrude","SWEPT_FACE",FACE,{"disambiguationData":[OSD([sQuery(id+"F2.wireOp",EDGE,"E3.12.0.0")])]})]});
            var Q122;
            {var subQ0=sQuery(id+"F0.wireOp",EDGE,"E1");Q122=makeQuery(id+"F3.boolean.opBoolean","SPLIT",EDGE,{"disambiguationData":[TD([makeQuery(id+"F3.opExtrude","SWEPT_FACE",FACE,{"disambiguationData":[OSD([sQuery(id+"F2.wireOp",EDGE,"E3.4.0.2")])]})])],"derivedFrom":makeQuery(id+"F1.opExtrude","CAP_EDGE",EDGE,{"disambiguationData":[OSD([subQ0])],"isStart":false})});}
            var Q123;
            {var subQ0=sQuery(id+"F0.wireOp",EDGE,"E1");Q123=makeQuery(id+"F3.boolean.opBoolean","SPLIT",EDGE,{"disambiguationData":[TD([makeQuery(id+"F3.opExtrude","SWEPT_FACE",FACE,{"disambiguationData":[OSD([sQuery(id+"F2.wireOp",EDGE,"E3.1.0.2")])]})])],"derivedFrom":makeQuery(id+"F1.opExtrude","CAP_EDGE",EDGE,{"disambiguationData":[OSD([subQ0])],"isStart":true})});}
            var Q124;
            {var subQ0=sQuery(id+"F0.wireOp",EDGE,"E1");Q124=makeQuery(id+"F3.boolean.opBoolean","SPLIT",EDGE,{"disambiguationData":[TD([makeQuery(id+"F3.opExtrude","SWEPT_FACE",FACE,{"disambiguationData":[OSD([sQuery(id+"F2.wireOp",EDGE,"E4.6.17.0")])]})])],"derivedFrom":makeQuery(id+"F1.opExtrude","CAP_EDGE",EDGE,{"disambiguationData":[OSD([subQ0])],"isStart":true})});}
            var Q125;
            Q125=makeQuery(id+"F3.boolean.opBoolean","COPY",FACE,{"derivedFrom":makeQuery(id+"F3.opExtrude","SWEPT_FACE",FACE,{"disambiguationData":[OSD([sQuery(id+"F2.wireOp",EDGE,"E3.5.0.1")])]})});
            var Q126;
            {var subQ0=sQuery(id+"F0.wireOp",EDGE,"E1");Q126=makeQuery(id+"F3.boolean.opBoolean","SPLIT",FACE,{"disambiguationData":[TD([makeQuery(id+"F3.opExtrude","SWEPT_FACE",FACE,{"disambiguationData":[OSD([sQuery(id+"F2.wireOp",EDGE,"E2.right")])]})])],"derivedFrom":makeQuery(id+"F1.opExtrude","SWEPT_FACE",FACE,{"disambiguationData":[OSD([subQ0])]})});}
            var Q127;
            {var subQ0=sQuery(id+"F0.wireOp",EDGE,"E1");Q127=makeQuery(id+"F3.boolean.opBoolean","SPLIT",FACE,{"disambiguationData":[TD([makeQuery(id+"F3.opExtrude","SWEPT_FACE",FACE,{"disambiguationData":[OSD([sQuery(id+"F2.wireOp",EDGE,"E4.6.16.0")])]})])],"derivedFrom":makeQuery(id+"F1.opExtrude","SWEPT_FACE",FACE,{"disambiguationData":[OSD([subQ0])]})});}
            var Q128;
            Q128=makeQuery(id+"F3.boolean.opBoolean","COPY",EDGE,{"derivedFrom":makeQuery(id+"F3.opExtrude","SWEPT_EDGE",EDGE,{"disambiguationData":[OSD([sQuery(id+"F2.wireOp",EDGE,"E3.8.0.1"),sQuery(id+"F2.wireOp",EDGE,"E3.8.0.2")])]})});
            var Q129;
            Q129=makeQuery(id+"F3.boolean.opBoolean","INTERSECT",EDGE,{"derivedFrom":[makeQuery(id+"F1.opExtrude","CAP_FACE",FACE,{"disambiguationData":[OSD([sQuery(id+"F0.wireOp",EDGE,"E0"),sQuery(id+"F0.wireOp",EDGE,"E1")])],"isStart":true}),makeQuery(id+"F3.opExtrude","SWEPT_FACE",FACE,{"disambiguationData":[OSD([sQuery(id+"F2.wireOp",EDGE,"E3.1.0.2")])]})]});
            var Q130;
            Q130=makeQuery(id+"F3.boolean.opBoolean","INTERSECT",EDGE,{"derivedFrom":[makeQuery(id+"F1.opExtrude","CAP_FACE",FACE,{"disambiguationData":[OSD([sQuery(id+"F0.wireOp",EDGE,"E0"),sQuery(id+"F0.wireOp",EDGE,"E1")])],"isStart":true}),makeQuery(id+"F3.opExtrude","SWEPT_FACE",FACE,{"disambiguationData":[OSD([sQuery(id+"F2.wireOp",EDGE,"E3.7.0.0")])]})]});
            var Q131;
            Q131=makeQuery(id+"F3.boolean.opBoolean","INTERSECT",EDGE,{"derivedFrom":[makeQuery(id+"F1.opExtrude","CAP_FACE",FACE,{"disambiguationData":[OSD([sQuery(id+"F0.wireOp",EDGE,"E0"),sQuery(id+"F0.wireOp",EDGE,"E1")])],"isStart":true}),makeQuery(id+"F3.opExtrude","SWEPT_FACE",FACE,{"disambiguationData":[OSD([sQuery(id+"F2.wireOp",EDGE,"E4.6.17.0")])]})]});
            var Q132;
            {var subQ0=sQuery(id+"F0.wireOp",EDGE,"E1");Q132=makeQuery(id+"F3.boolean.opBoolean","SPLIT",EDGE,{"disambiguationData":[TD([makeQuery(id+"F3.opExtrude","SWEPT_FACE",FACE,{"disambiguationData":[OSD([sQuery(id+"F2.wireOp",EDGE,"E3.5.0.2")])]})])],"derivedFrom":makeQuery(id+"F1.opExtrude","CAP_EDGE",EDGE,{"disambiguationData":[OSD([subQ0])],"isStart":false})});}
            var Q133;
            {var subQ0=sQuery(id+"F0.wireOp",EDGE,"E1");Q133=makeQuery(id+"F3.boolean.opBoolean","SPLIT",EDGE,{"disambiguationData":[TD([makeQuery(id+"F3.opExtrude","SWEPT_FACE",FACE,{"disambiguationData":[OSD([sQuery(id+"F2.wireOp",EDGE,"E3.2.0.2")])]})])],"derivedFrom":makeQuery(id+"F1.opExtrude","CAP_EDGE",EDGE,{"disambiguationData":[OSD([subQ0])],"isStart":true})});}
            var Q134;
            {var subQ0=sQuery(id+"F0.wireOp",EDGE,"E1");Q134=makeQuery(id+"F3.boolean.opBoolean","SPLIT",EDGE,{"disambiguationData":[TD([makeQuery(id+"F3.opExtrude","SWEPT_FACE",FACE,{"disambiguationData":[OSD([sQuery(id+"F2.wireOp",EDGE,"E5.6.18.0")])]})])],"derivedFrom":makeQuery(id+"F1.opExtrude","CAP_EDGE",EDGE,{"disambiguationData":[OSD([subQ0])],"isStart":true})});}
            var Q135;
            Q135=makeQuery(id+"F3.boolean.opBoolean","COPY",FACE,{"derivedFrom":makeQuery(id+"F3.opExtrude","SWEPT_FACE",FACE,{"disambiguationData":[OSD([sQuery(id+"F2.wireOp",EDGE,"E3.11.0.0")])]})});
            var Q136;
            Q136=makeQuery(id+"F3.boolean.opBoolean","COPY",FACE,{"derivedFrom":makeQuery(id+"F3.opExtrude","SWEPT_FACE",FACE,{"disambiguationData":[OSD([sQuery(id+"F2.wireOp",EDGE,"E4.3.16.0")])]})});
            var Q137;
            {var subQ0=sQuery(id+"F0.wireOp",EDGE,"E1");Q137=makeQuery(id+"F3.boolean.opBoolean","SPLIT",FACE,{"disambiguationData":[TD([makeQuery(id+"F3.opExtrude","SWEPT_FACE",FACE,{"disambiguationData":[OSD([sQuery(id+"F2.wireOp",EDGE,"E4.6.17.0")])]})])],"derivedFrom":makeQuery(id+"F1.opExtrude","SWEPT_FACE",FACE,{"disambiguationData":[OSD([subQ0])]})});}
            var Q138;
            Q138=makeQuery(id+"F3.boolean.opBoolean","COPY",EDGE,{"derivedFrom":makeQuery(id+"F3.opExtrude","CAP_EDGE",EDGE,{"disambiguationData":[OSD([sQuery(id+"F2.wireOp",EDGE,"E3.6.0.0")])],"isStart":true})});
            var Q139;
            Q139=makeQuery(id+"F3.boolean.opBoolean","COPY",EDGE,{"derivedFrom":makeQuery(id+"F3.opExtrude","CAP_EDGE",EDGE,{"disambiguationData":[OSD([sQuery(id+"F2.wireOp",EDGE,"E4.6.16.0")])],"isStart":true})});
            var Q140;
            Q140=makeQuery(id+"F3.boolean.opBoolean","INTERSECT",EDGE,{"derivedFrom":[makeQuery(id+"F1.opExtrude","CAP_FACE",FACE,{"disambiguationData":[OSD([sQuery(id+"F0.wireOp",EDGE,"E0"),sQuery(id+"F0.wireOp",EDGE,"E1")])],"isStart":true}),makeQuery(id+"F3.opExtrude","SWEPT_FACE",FACE,{"disambiguationData":[OSD([sQuery(id+"F2.wireOp",EDGE,"E3.2.0.0")])]})]});
            var Q141;
            Q141=makeQuery(id+"F3.boolean.opBoolean","INTERSECT",EDGE,{"derivedFrom":[makeQuery(id+"F1.opExtrude","CAP_FACE",FACE,{"disambiguationData":[OSD([sQuery(id+"F0.wireOp",EDGE,"E0"),sQuery(id+"F0.wireOp",EDGE,"E1")])],"isStart":true}),makeQuery(id+"F3.opExtrude","SWEPT_FACE",FACE,{"disambiguationData":[OSD([sQuery(id+"F2.wireOp",EDGE,"E3.12.0.2")])]})]});
            var Q142;
            {var subQ0=sQuery(id+"F0.wireOp",EDGE,"E1");Q142=makeQuery(id+"F3.boolean.opBoolean","SPLIT",EDGE,{"disambiguationData":[TD([makeQuery(id+"F3.opExtrude","SWEPT_FACE",FACE,{"disambiguationData":[OSD([sQuery(id+"F2.wireOp",EDGE,"E3.6.0.2")])]})])],"derivedFrom":makeQuery(id+"F1.opExtrude","CAP_EDGE",EDGE,{"disambiguationData":[OSD([subQ0])],"isStart":false})});}
            var Q143;
            {var subQ0=sQuery(id+"F0.wireOp",EDGE,"E1");Q143=makeQuery(id+"F3.boolean.opBoolean","SPLIT",EDGE,{"disambiguationData":[TD([makeQuery(id+"F3.opExtrude","SWEPT_FACE",FACE,{"disambiguationData":[OSD([sQuery(id+"F2.wireOp",EDGE,"E3.3.0.2")])]})])],"derivedFrom":makeQuery(id+"F1.opExtrude","CAP_EDGE",EDGE,{"disambiguationData":[OSD([subQ0])],"isStart":true})});}
            var Q144;
            Q144=makeQuery(id+"F3.boolean.opBoolean","COPY",FACE,{"derivedFrom":makeQuery(id+"F3.opExtrude","SWEPT_FACE",FACE,{"disambiguationData":[OSD([sQuery(id+"F2.wireOp",EDGE,"E3.11.0.1")])]})});
            var Q145;
            {var subQ0=sQuery(id+"F0.wireOp",EDGE,"E1");Q145=makeQuery(id+"F3.boolean.opBoolean","SPLIT",FACE,{"disambiguationData":[TD([makeQuery(id+"F3.opExtrude","SWEPT_FACE",FACE,{"disambiguationData":[OSD([sQuery(id+"F2.wireOp",EDGE,"E3.2.0.2")])]})])],"derivedFrom":makeQuery(id+"F1.opExtrude","SWEPT_FACE",FACE,{"disambiguationData":[OSD([subQ0])]})});}
            var Q146;
            {var subQ0=sQuery(id+"F0.wireOp",EDGE,"E1");Q146=makeQuery(id+"F3.boolean.opBoolean","SPLIT",FACE,{"disambiguationData":[TD([makeQuery(id+"F3.opExtrude","SWEPT_FACE",FACE,{"disambiguationData":[OSD([sQuery(id+"F2.wireOp",EDGE,"E5.6.18.0")])]})])],"derivedFrom":makeQuery(id+"F1.opExtrude","SWEPT_FACE",FACE,{"disambiguationData":[OSD([subQ0])]})});}
            var Q147;
            Q147=makeQuery(id+"F3.boolean.opBoolean","COPY",EDGE,{"derivedFrom":makeQuery(id+"F3.opExtrude","SWEPT_EDGE",EDGE,{"disambiguationData":[OSD([sQuery(id+"F2.wireOp",EDGE,"E3.9.0.1"),sQuery(id+"F2.wireOp",EDGE,"E3.9.0.2")])]})});
            var Q148;
            Q148=makeQuery(id+"F3.boolean.opBoolean","COPY",EDGE,{"derivedFrom":makeQuery(id+"F3.opExtrude","SWEPT_EDGE",EDGE,{"disambiguationData":[OSD([sQuery(id+"F2.wireOp",EDGE,"E4.3.17.0"),sQuery(id+"F2.wireOp",EDGE,"E4.6.17.0")])]})});
            var Q149;
            Q149=makeQuery(id+"F3.boolean.opBoolean","INTERSECT",EDGE,{"derivedFrom":[makeQuery(id+"F1.opExtrude","CAP_FACE",FACE,{"disambiguationData":[OSD([sQuery(id+"F0.wireOp",EDGE,"E0"),sQuery(id+"F0.wireOp",EDGE,"E1")])],"isStart":true}),makeQuery(id+"F3.opExtrude","SWEPT_FACE",FACE,{"disambiguationData":[OSD([sQuery(id+"F2.wireOp",EDGE,"E3.7.0.2")])]})]});
            var Q150;
            Q150=makeQuery(id+"F3.boolean.opBoolean","INTERSECT",EDGE,{"derivedFrom":[makeQuery(id+"F1.opExtrude","CAP_FACE",FACE,{"disambiguationData":[OSD([sQuery(id+"F0.wireOp",EDGE,"E0"),sQuery(id+"F0.wireOp",EDGE,"E1")])],"isStart":true}),makeQuery(id+"F3.opExtrude","SWEPT_FACE",FACE,{"disambiguationData":[OSD([sQuery(id+"F2.wireOp",EDGE,"E3.13.0.0")])]})]});
            var Q151;
            {var subQ0=sQuery(id+"F0.wireOp",EDGE,"E1");Q151=makeQuery(id+"F3.boolean.opBoolean","SPLIT",EDGE,{"disambiguationData":[TD([makeQuery(id+"F3.opExtrude","SWEPT_FACE",FACE,{"disambiguationData":[OSD([sQuery(id+"F2.wireOp",EDGE,"E3.7.0.2")])]})])],"derivedFrom":makeQuery(id+"F1.opExtrude","CAP_EDGE",EDGE,{"disambiguationData":[OSD([subQ0])],"isStart":false})});}
            var Q152;
            {var subQ0=sQuery(id+"F0.wireOp",EDGE,"E1");Q152=makeQuery(id+"F3.boolean.opBoolean","SPLIT",EDGE,{"disambiguationData":[TD([makeQuery(id+"F3.opExtrude","SWEPT_FACE",FACE,{"disambiguationData":[OSD([sQuery(id+"F2.wireOp",EDGE,"E3.4.0.2")])]})])],"derivedFrom":makeQuery(id+"F1.opExtrude","CAP_EDGE",EDGE,{"disambiguationData":[OSD([subQ0])],"isStart":true})});}
            var Q153;
            Q153=makeQuery(id+"F3.boolean.opBoolean","COPY",FACE,{"derivedFrom":makeQuery(id+"F3.opExtrude","SWEPT_FACE",FACE,{"disambiguationData":[OSD([sQuery(id+"F2.wireOp",EDGE,"E3.6.0.1")])]})});
            var Q154;
            {var subQ0=sQuery(id+"F0.wireOp",EDGE,"E1");Q154=makeQuery(id+"F3.boolean.opBoolean","SPLIT",FACE,{"disambiguationData":[TD([makeQuery(id+"F3.opExtrude","SWEPT_FACE",FACE,{"disambiguationData":[OSD([sQuery(id+"F2.wireOp",EDGE,"E3.3.0.2")])]})])],"derivedFrom":makeQuery(id+"F1.opExtrude","SWEPT_FACE",FACE,{"disambiguationData":[OSD([subQ0])]})});}
            var Q155;
            Q155=makeQuery(id+"F3.boolean.opBoolean","COPY",EDGE,{"derivedFrom":makeQuery(id+"F3.opExtrude","CAP_EDGE",EDGE,{"disambiguationData":[OSD([sQuery(id+"F2.wireOp",EDGE,"E3.6.0.2")])],"isStart":true})});
            var Q156;
            Q156=makeQuery(id+"F3.boolean.opBoolean","INTERSECT",EDGE,{"derivedFrom":[makeQuery(id+"F1.opExtrude","CAP_FACE",FACE,{"disambiguationData":[OSD([sQuery(id+"F0.wireOp",EDGE,"E0"),sQuery(id+"F0.wireOp",EDGE,"E1")])],"isStart":true}),makeQuery(id+"F3.opExtrude","SWEPT_FACE",FACE,{"disambiguationData":[OSD([sQuery(id+"F2.wireOp",EDGE,"E3.2.0.2")])]})]});
            var Q157;
            {var subQ0=sQuery(id+"F0.wireOp",EDGE,"E1");Q157=makeQuery(id+"F3.boolean.opBoolean","SPLIT",EDGE,{"disambiguationData":[TD([makeQuery(id+"F3.opExtrude","SWEPT_FACE",FACE,{"disambiguationData":[OSD([sQuery(id+"F2.wireOp",EDGE,"E3.8.0.2")])]})])],"derivedFrom":makeQuery(id+"F1.opExtrude","CAP_EDGE",EDGE,{"disambiguationData":[OSD([subQ0])],"isStart":false})});}
            var Q158;
            {var subQ0=sQuery(id+"F0.wireOp",EDGE,"E1");Q158=makeQuery(id+"F3.boolean.opBoolean","SPLIT",EDGE,{"disambiguationData":[TD([makeQuery(id+"F3.opExtrude","SWEPT_FACE",FACE,{"disambiguationData":[OSD([sQuery(id+"F2.wireOp",EDGE,"E3.5.0.2")])]})])],"derivedFrom":makeQuery(id+"F1.opExtrude","CAP_EDGE",EDGE,{"disambiguationData":[OSD([subQ0])],"isStart":true})});}
            var Q159;
            Q159=makeQuery(id+"F3.boolean.opBoolean","COPY",FACE,{"derivedFrom":makeQuery(id+"F3.opExtrude","SWEPT_FACE",FACE,{"disambiguationData":[OSD([sQuery(id+"F2.wireOp",EDGE,"E4.3.17.0")])]})});
            var Q160;
            {var subQ0=sQuery(id+"F0.wireOp",EDGE,"E1");Q160=makeQuery(id+"F3.boolean.opBoolean","SPLIT",FACE,{"disambiguationData":[TD([makeQuery(id+"F3.opExtrude","SWEPT_FACE",FACE,{"disambiguationData":[OSD([sQuery(id+"F2.wireOp",EDGE,"E3.4.0.2")])]})])],"derivedFrom":makeQuery(id+"F1.opExtrude","SWEPT_FACE",FACE,{"disambiguationData":[OSD([subQ0])]})});}
            var Q161;
            Q161=makeQuery(id+"F3.boolean.opBoolean","COPY",EDGE,{"derivedFrom":makeQuery(id+"F3.opExtrude","SWEPT_EDGE",EDGE,{"disambiguationData":[OSD([sQuery(id+"F2.wireOp",EDGE,"E3.10.0.1"),sQuery(id+"F2.wireOp",EDGE,"E3.10.0.2")])]})});
            var Q162;
            Q162=makeQuery(id+"F3.boolean.opBoolean","COPY",EDGE,{"derivedFrom":makeQuery(id+"F3.opExtrude","CAP_EDGE",EDGE,{"disambiguationData":[OSD([sQuery(id+"F2.wireOp",EDGE,"E3.1.0.2")])],"isStart":true})});
            var Q163;
            Q163=makeQuery(id+"F3.boolean.opBoolean","INTERSECT",EDGE,{"derivedFrom":[makeQuery(id+"F1.opExtrude","CAP_FACE",FACE,{"disambiguationData":[OSD([sQuery(id+"F0.wireOp",EDGE,"E0"),sQuery(id+"F0.wireOp",EDGE,"E1")])],"isStart":true}),makeQuery(id+"F3.opExtrude","SWEPT_FACE",FACE,{"disambiguationData":[OSD([sQuery(id+"F2.wireOp",EDGE,"E3.3.0.0")])]})]});
            var Q164;
            Q164=makeQuery(id+"F3.boolean.opBoolean","INTERSECT",EDGE,{"derivedFrom":[makeQuery(id+"F1.opExtrude","CAP_FACE",FACE,{"disambiguationData":[OSD([sQuery(id+"F0.wireOp",EDGE,"E0"),sQuery(id+"F0.wireOp",EDGE,"E1")])],"isStart":true}),makeQuery(id+"F3.opExtrude","SWEPT_FACE",FACE,{"disambiguationData":[OSD([sQuery(id+"F2.wireOp",EDGE,"E3.13.0.2")])]})]});
            var Q165;
            Q165=makeQuery(id+"F3.boolean.opBoolean","INTERSECT",EDGE,{"derivedFrom":[makeQuery(id+"F1.opExtrude","CAP_FACE",FACE,{"disambiguationData":[OSD([sQuery(id+"F0.wireOp",EDGE,"E0"),sQuery(id+"F0.wireOp",EDGE,"E1")])],"isStart":true}),makeQuery(id+"F3.opExtrude","SWEPT_FACE",FACE,{"disambiguationData":[OSD([sQuery(id+"F2.wireOp",EDGE,"E5.0.19.0")])]})]});
            var Q166;
            {var subQ0=sQuery(id+"F0.wireOp",EDGE,"E1");Q166=makeQuery(id+"F3.boolean.opBoolean","SPLIT",EDGE,{"disambiguationData":[TD([makeQuery(id+"F3.opExtrude","SWEPT_FACE",FACE,{"disambiguationData":[OSD([sQuery(id+"F2.wireOp",EDGE,"E3.9.0.2")])]})])],"derivedFrom":makeQuery(id+"F1.opExtrude","CAP_EDGE",EDGE,{"disambiguationData":[OSD([subQ0])],"isStart":false})});}
            var Q167;
            {var subQ0=sQuery(id+"F0.wireOp",EDGE,"E1");Q167=makeQuery(id+"F3.boolean.opBoolean","SPLIT",EDGE,{"disambiguationData":[TD([makeQuery(id+"F3.opExtrude","SWEPT_FACE",FACE,{"disambiguationData":[OSD([sQuery(id+"F2.wireOp",EDGE,"E3.6.0.2")])]})])],"derivedFrom":makeQuery(id+"F1.opExtrude","CAP_EDGE",EDGE,{"disambiguationData":[OSD([subQ0])],"isStart":true})});}
            var Q168;
            Q168=makeQuery(id+"F3.boolean.opBoolean","COPY",FACE,{"derivedFrom":makeQuery(id+"F3.opExtrude","SWEPT_FACE",FACE,{"disambiguationData":[OSD([sQuery(id+"F2.wireOp",EDGE,"E3.12.0.1")])]})});
            var Q169;
            {var subQ0=sQuery(id+"F0.wireOp",EDGE,"E1");Q169=makeQuery(id+"F3.boolean.opBoolean","SPLIT",FACE,{"disambiguationData":[TD([makeQuery(id+"F3.opExtrude","SWEPT_FACE",FACE,{"disambiguationData":[OSD([sQuery(id+"F2.wireOp",EDGE,"E3.5.0.2")])]})])],"derivedFrom":makeQuery(id+"F1.opExtrude","SWEPT_FACE",FACE,{"disambiguationData":[OSD([subQ0])]})});}
            var Q170;
            Q170=makeQuery(id+"F3.boolean.opBoolean","INTERSECT",EDGE,{"derivedFrom":[makeQuery(id+"F1.opExtrude","CAP_FACE",FACE,{"disambiguationData":[OSD([sQuery(id+"F0.wireOp",EDGE,"E0"),sQuery(id+"F0.wireOp",EDGE,"E1")])],"isStart":true}),makeQuery(id+"F3.opExtrude","SWEPT_FACE",FACE,{"disambiguationData":[OSD([sQuery(id+"F2.wireOp",EDGE,"E3.8.0.2")])]})]});
            var Q171;
            Q171=makeQuery(id+"F3.boolean.opBoolean","INTERSECT",EDGE,{"derivedFrom":[makeQuery(id+"F1.opExtrude","CAP_FACE",FACE,{"disambiguationData":[OSD([sQuery(id+"F0.wireOp",EDGE,"E0"),sQuery(id+"F0.wireOp",EDGE,"E1")])],"isStart":true}),makeQuery(id+"F3.opExtrude","SWEPT_FACE",FACE,{"disambiguationData":[OSD([sQuery(id+"F2.wireOp",EDGE,"E3.14.0.0")])]})]});
            var Q172;
            {var subQ0=sQuery(id+"F0.wireOp",EDGE,"E1");Q172=makeQuery(id+"F3.boolean.opBoolean","SPLIT",EDGE,{"disambiguationData":[TD([makeQuery(id+"F3.opExtrude","SWEPT_FACE",FACE,{"disambiguationData":[OSD([sQuery(id+"F2.wireOp",EDGE,"E3.10.0.2")])]})])],"derivedFrom":makeQuery(id+"F1.opExtrude","CAP_EDGE",EDGE,{"disambiguationData":[OSD([subQ0])],"isStart":false})});}
            var Q173;
            {var subQ0=sQuery(id+"F0.wireOp",EDGE,"E1");Q173=makeQuery(id+"F3.boolean.opBoolean","SPLIT",EDGE,{"disambiguationData":[TD([makeQuery(id+"F3.opExtrude","SWEPT_FACE",FACE,{"disambiguationData":[OSD([sQuery(id+"F2.wireOp",EDGE,"E3.7.0.2")])]})])],"derivedFrom":makeQuery(id+"F1.opExtrude","CAP_EDGE",EDGE,{"disambiguationData":[OSD([subQ0])],"isStart":true})});}
            var Q174;
            Q174=makeQuery(id+"F3.boolean.opBoolean","COPY",FACE,{"derivedFrom":makeQuery(id+"F3.opExtrude","SWEPT_FACE",FACE,{"disambiguationData":[OSD([sQuery(id+"F2.wireOp",EDGE,"E3.7.0.1")])]})});
            var Q175;
            {var subQ0=sQuery(id+"F0.wireOp",EDGE,"E1");Q175=makeQuery(id+"F3.boolean.opBoolean","SPLIT",FACE,{"disambiguationData":[TD([makeQuery(id+"F3.opExtrude","SWEPT_FACE",FACE,{"disambiguationData":[OSD([sQuery(id+"F2.wireOp",EDGE,"E3.6.0.2")])]})])],"derivedFrom":makeQuery(id+"F1.opExtrude","SWEPT_FACE",FACE,{"disambiguationData":[OSD([subQ0])]})});}
            var Q176;
            Q176=makeQuery(id+"F3.boolean.opBoolean","COPY",EDGE,{"derivedFrom":makeQuery(id+"F3.opExtrude","SWEPT_EDGE",EDGE,{"disambiguationData":[OSD([sQuery(id+"F2.wireOp",EDGE,"E3.11.0.1"),sQuery(id+"F2.wireOp",EDGE,"E3.11.0.2")])]})});
            var Q177;
            Q177=makeQuery(id+"F3.boolean.opBoolean","COPY",EDGE,{"derivedFrom":makeQuery(id+"F3.opExtrude","SWEPT_EDGE",EDGE,{"disambiguationData":[OSD([sQuery(id+"F2.wireOp",EDGE,"E5.3.19.0"),sQuery(id+"F2.wireOp",EDGE,"E5.6.19.0")])]})});
            var Q178;
            Q178=makeQuery(id+"F3.boolean.opBoolean","INTERSECT",EDGE,{"derivedFrom":[makeQuery(id+"F1.opExtrude","CAP_FACE",FACE,{"disambiguationData":[OSD([sQuery(id+"F0.wireOp",EDGE,"E0"),sQuery(id+"F0.wireOp",EDGE,"E1")])],"isStart":true}),makeQuery(id+"F3.opExtrude","SWEPT_FACE",FACE,{"disambiguationData":[OSD([sQuery(id+"F2.wireOp",EDGE,"E3.3.0.2")])]})]});
            var Q179;
            Q179=makeQuery(id+"F3.boolean.opBoolean","INTERSECT",EDGE,{"derivedFrom":[makeQuery(id+"F1.opExtrude","CAP_FACE",FACE,{"disambiguationData":[OSD([sQuery(id+"F0.wireOp",EDGE,"E0"),sQuery(id+"F0.wireOp",EDGE,"E1")])],"isStart":true}),makeQuery(id+"F3.opExtrude","SWEPT_FACE",FACE,{"disambiguationData":[OSD([sQuery(id+"F2.wireOp",EDGE,"E3.9.0.0")])]})]});
            var Q180;
            Q180=makeQuery(id+"F3.boolean.opBoolean","INTERSECT",EDGE,{"derivedFrom":[makeQuery(id+"F1.opExtrude","CAP_FACE",FACE,{"disambiguationData":[OSD([sQuery(id+"F0.wireOp",EDGE,"E0"),sQuery(id+"F0.wireOp",EDGE,"E1")])],"isStart":true}),makeQuery(id+"F3.opExtrude","SWEPT_FACE",FACE,{"disambiguationData":[OSD([sQuery(id+"F2.wireOp",EDGE,"E5.6.19.0")])]})]});
            var Q181;
            {var subQ0=sQuery(id+"F0.wireOp",EDGE,"E1");Q181=makeQuery(id+"F3.boolean.opBoolean","SPLIT",EDGE,{"disambiguationData":[TD([makeQuery(id+"F3.opExtrude","SWEPT_FACE",FACE,{"disambiguationData":[OSD([sQuery(id+"F2.wireOp",EDGE,"E3.11.0.2")])]})])],"derivedFrom":makeQuery(id+"F1.opExtrude","CAP_EDGE",EDGE,{"disambiguationData":[OSD([subQ0])],"isStart":false})});}
            var Q182;
            {var subQ0=sQuery(id+"F0.wireOp",EDGE,"E1");Q182=makeQuery(id+"F3.boolean.opBoolean","SPLIT",EDGE,{"disambiguationData":[TD([makeQuery(id+"F3.opExtrude","SWEPT_FACE",FACE,{"disambiguationData":[OSD([sQuery(id+"F2.wireOp",EDGE,"E3.8.0.2")])]})])],"derivedFrom":makeQuery(id+"F1.opExtrude","CAP_EDGE",EDGE,{"disambiguationData":[OSD([subQ0])],"isStart":true})});}
            var Q183;
            Q183=makeQuery(id+"F3.boolean.opBoolean","COPY",FACE,{"derivedFrom":makeQuery(id+"F3.opExtrude","SWEPT_FACE",FACE,{"disambiguationData":[OSD([sQuery(id+"F2.wireOp",EDGE,"E5.3.18.0")])]})});
            var Q184;
            {var subQ0=sQuery(id+"F0.wireOp",EDGE,"E1");Q184=makeQuery(id+"F3.boolean.opBoolean","SPLIT",FACE,{"disambiguationData":[TD([makeQuery(id+"F3.opExtrude","SWEPT_FACE",FACE,{"disambiguationData":[OSD([sQuery(id+"F2.wireOp",EDGE,"E3.7.0.2")])]})])],"derivedFrom":makeQuery(id+"F1.opExtrude","SWEPT_FACE",FACE,{"disambiguationData":[OSD([subQ0])]})});}
            var Q185;
            Q185=makeQuery(id+"F3.boolean.opBoolean","COPY",EDGE,{"derivedFrom":makeQuery(id+"F3.opExtrude","SWEPT_EDGE",EDGE,{"disambiguationData":[OSD([sQuery(id+"F0.wireOp",EDGE,"E1"),sQuery(id+"F2.wireOp",EDGE,"E2.left")])]})});
            var Q186;
            Q186=makeQuery(id+"F3.boolean.opBoolean","COPY",EDGE,{"derivedFrom":makeQuery(id+"F3.opExtrude","CAP_EDGE",EDGE,{"disambiguationData":[OSD([sQuery(id+"F2.wireOp",EDGE,"E5.6.18.0")])],"isStart":true})});
            var Q187;
            Q187=makeQuery(id+"F3.boolean.opBoolean","INTERSECT",EDGE,{"derivedFrom":[makeQuery(id+"F1.opExtrude","CAP_FACE",FACE,{"disambiguationData":[OSD([sQuery(id+"F0.wireOp",EDGE,"E0"),sQuery(id+"F0.wireOp",EDGE,"E1")])],"isStart":true}),makeQuery(id+"F3.opExtrude","SWEPT_FACE",FACE,{"disambiguationData":[OSD([sQuery(id+"F2.wireOp",EDGE,"E3.4.0.0")])]})]});
            var Q188;
            Q188=makeQuery(id+"F3.boolean.opBoolean","INTERSECT",EDGE,{"derivedFrom":[makeQuery(id+"F1.opExtrude","CAP_FACE",FACE,{"disambiguationData":[OSD([sQuery(id+"F0.wireOp",EDGE,"E0"),sQuery(id+"F0.wireOp",EDGE,"E1")])],"isStart":true}),makeQuery(id+"F3.opExtrude","SWEPT_FACE",FACE,{"disambiguationData":[OSD([sQuery(id+"F2.wireOp",EDGE,"E3.14.0.2")])]})]});
            var Q189;
            {var subQ0=sQuery(id+"F0.wireOp",EDGE,"E1");Q189=makeQuery(id+"F3.boolean.opBoolean","SPLIT",EDGE,{"disambiguationData":[TD([makeQuery(id+"F3.opExtrude","SWEPT_FACE",FACE,{"disambiguationData":[OSD([sQuery(id+"F2.wireOp",EDGE,"E3.12.0.2")])]})])],"derivedFrom":makeQuery(id+"F1.opExtrude","CAP_EDGE",EDGE,{"disambiguationData":[OSD([subQ0])],"isStart":false})});}
            var Q190;
            {var subQ0=sQuery(id+"F0.wireOp",EDGE,"E1");Q190=makeQuery(id+"F3.boolean.opBoolean","SPLIT",EDGE,{"disambiguationData":[TD([makeQuery(id+"F3.opExtrude","SWEPT_FACE",FACE,{"disambiguationData":[OSD([sQuery(id+"F2.wireOp",EDGE,"E3.9.0.2")])]})])],"derivedFrom":makeQuery(id+"F1.opExtrude","CAP_EDGE",EDGE,{"disambiguationData":[OSD([subQ0])],"isStart":true})});}
            var Q191;
            Q191=makeQuery(id+"F3.boolean.opBoolean","COPY",FACE,{"derivedFrom":makeQuery(id+"F3.opExtrude","SWEPT_FACE",FACE,{"disambiguationData":[OSD([sQuery(id+"F2.wireOp",EDGE,"E3.13.0.1")])]})});
            var Q192;
            Q192=makeQuery(id+"F3.boolean.opBoolean","COPY",FACE,{"derivedFrom":makeQuery(id+"F3.opExtrude","SWEPT_FACE",FACE,{"disambiguationData":[OSD([sQuery(id+"F2.wireOp",EDGE,"E5.6.18.0")])]})});
            var Q193;
            {var subQ0=sQuery(id+"F0.wireOp",EDGE,"E1");Q193=makeQuery(id+"F3.boolean.opBoolean","SPLIT",FACE,{"disambiguationData":[TD([makeQuery(id+"F3.opExtrude","SWEPT_FACE",FACE,{"disambiguationData":[OSD([sQuery(id+"F2.wireOp",EDGE,"E3.8.0.2")])]})])],"derivedFrom":makeQuery(id+"F1.opExtrude","SWEPT_FACE",FACE,{"disambiguationData":[OSD([subQ0])]})});}
            var Q194;
            Q194=makeQuery(id+"F3.boolean.opBoolean","COPY",EDGE,{"derivedFrom":makeQuery(id+"F3.opExtrude","SWEPT_EDGE",EDGE,{"disambiguationData":[OSD([sQuery(id+"F2.wireOp",EDGE,"E3.12.0.1"),sQuery(id+"F2.wireOp",EDGE,"E3.12.0.2")])]})});
            var Q195;
            Q195=makeQuery(id+"F3.boolean.opBoolean","INTERSECT",EDGE,{"derivedFrom":[makeQuery(id+"F1.opExtrude","CAP_FACE",FACE,{"disambiguationData":[OSD([sQuery(id+"F0.wireOp",EDGE,"E0"),sQuery(id+"F0.wireOp",EDGE,"E1")])],"isStart":true}),makeQuery(id+"F3.opExtrude","SWEPT_FACE",FACE,{"disambiguationData":[OSD([sQuery(id+"F2.wireOp",EDGE,"E3.9.0.2")])]})]});
            var Q196;
            Q196=makeQuery(id+"F3.boolean.opBoolean","INTERSECT",EDGE,{"derivedFrom":[makeQuery(id+"F1.opExtrude","CAP_FACE",FACE,{"disambiguationData":[OSD([sQuery(id+"F0.wireOp",EDGE,"E0"),sQuery(id+"F0.wireOp",EDGE,"E1")])],"isStart":true}),makeQuery(id+"F3.opExtrude","SWEPT_FACE",FACE,{"disambiguationData":[OSD([sQuery(id+"F2.wireOp",EDGE,"E4.0.15.0")])]})]});
            var Q197;
            {var subQ1=sQuery(id+"F0.wireOp",EDGE,"E1");Q197=makeQuery(id+"F3.boolean.opBoolean","SPLIT",EDGE,{"disambiguationData":[TD([makeQuery(id+"F3.opExtrude","SWEPT_FACE",FACE,{"disambiguationData":[OSD([sQuery(id+"F2.wireOp",EDGE,"E5.6.19.0")])]})])],"derivedFrom":makeQuery(id+"F1.opExtrude","CAP_EDGE",EDGE,{"disambiguationData":[OSD([subQ1])],"isStart":true})});}
            var Q198;
            {var subQ0=sQuery(id+"F0.wireOp",EDGE,"E1");Q198=makeQuery(id+"F3.boolean.opBoolean","SPLIT",EDGE,{"disambiguationData":[TD([makeQuery(id+"F3.opExtrude","SWEPT_FACE",FACE,{"disambiguationData":[OSD([sQuery(id+"F2.wireOp",EDGE,"E3.13.0.2")])]})])],"derivedFrom":makeQuery(id+"F1.opExtrude","CAP_EDGE",EDGE,{"disambiguationData":[OSD([subQ0])],"isStart":false})});}
            var Q199;
            {var subQ0=sQuery(id+"F0.wireOp",EDGE,"E1");Q199=makeQuery(id+"F3.boolean.opBoolean","SPLIT",EDGE,{"disambiguationData":[TD([makeQuery(id+"F3.opExtrude","SWEPT_FACE",FACE,{"disambiguationData":[OSD([sQuery(id+"F2.wireOp",EDGE,"E3.10.0.2")])]})])],"derivedFrom":makeQuery(id+"F1.opExtrude","CAP_EDGE",EDGE,{"disambiguationData":[OSD([subQ0])],"isStart":true})});}
            var Q200;
            Q200=makeQuery(id+"F3.boolean.opBoolean","COPY",FACE,{"derivedFrom":makeQuery(id+"F3.opExtrude","SWEPT_FACE",FACE,{"disambiguationData":[OSD([sQuery(id+"F2.wireOp",EDGE,"E3.8.0.1")])]})});
            var Q201;
            {var subQ0=sQuery(id+"F0.wireOp",EDGE,"E1");Q201=makeQuery(id+"F3.boolean.opBoolean","SPLIT",FACE,{"disambiguationData":[TD([makeQuery(id+"F3.opExtrude","SWEPT_FACE",FACE,{"disambiguationData":[OSD([sQuery(id+"F2.wireOp",EDGE,"E3.9.0.2")])]})])],"derivedFrom":makeQuery(id+"F1.opExtrude","SWEPT_FACE",FACE,{"disambiguationData":[OSD([subQ0])]})});}
            var Q202;
            Q202=makeQuery(id+"F3.boolean.opBoolean","INTERSECT",EDGE,{"derivedFrom":[makeQuery(id+"F1.opExtrude","CAP_FACE",FACE,{"disambiguationData":[OSD([sQuery(id+"F0.wireOp",EDGE,"E0"),sQuery(id+"F0.wireOp",EDGE,"E1")])],"isStart":true}),makeQuery(id+"F3.opExtrude","SWEPT_FACE",FACE,{"disambiguationData":[OSD([sQuery(id+"F2.wireOp",EDGE,"E3.4.0.2")])]})]});
            var Q203;
            Q203=makeQuery(id+"F3.boolean.opBoolean","INTERSECT",EDGE,{"derivedFrom":[makeQuery(id+"F1.opExtrude","CAP_FACE",FACE,{"disambiguationData":[OSD([sQuery(id+"F0.wireOp",EDGE,"E0"),sQuery(id+"F0.wireOp",EDGE,"E1")])],"isStart":true}),makeQuery(id+"F3.opExtrude","SWEPT_FACE",FACE,{"disambiguationData":[OSD([sQuery(id+"F2.wireOp",EDGE,"E3.10.0.0")])]})]});
            var Q204;
            {var subQ0=sQuery(id+"F0.wireOp",EDGE,"E1");Q204=makeQuery(id+"F3.boolean.opBoolean","SPLIT",EDGE,{"disambiguationData":[TD([makeQuery(id+"F3.opExtrude","SWEPT_FACE",FACE,{"disambiguationData":[OSD([sQuery(id+"F2.wireOp",EDGE,"E3.14.0.2")])]})])],"derivedFrom":makeQuery(id+"F1.opExtrude","CAP_EDGE",EDGE,{"disambiguationData":[OSD([subQ0])],"isStart":false})});}
            var Q205;
            {var subQ0=sQuery(id+"F0.wireOp",EDGE,"E1");Q205=makeQuery(id+"F3.boolean.opBoolean","SPLIT",EDGE,{"disambiguationData":[TD([makeQuery(id+"F3.opExtrude","SWEPT_FACE",FACE,{"disambiguationData":[OSD([sQuery(id+"F2.wireOp",EDGE,"E3.11.0.2")])]})])],"derivedFrom":makeQuery(id+"F1.opExtrude","CAP_EDGE",EDGE,{"disambiguationData":[OSD([subQ0])],"isStart":true})});}
            var Q206;
            Q206=makeQuery(id+"F3.boolean.opBoolean","COPY",FACE,{"derivedFrom":makeQuery(id+"F3.opExtrude","SWEPT_FACE",FACE,{"disambiguationData":[OSD([sQuery(id+"F2.wireOp",EDGE,"E3.8.0.2")])]})});
            var Q207;
            Q207=makeQuery(id+"F3.boolean.opBoolean","COPY",FACE,{"derivedFrom":makeQuery(id+"F3.opExtrude","SWEPT_FACE",FACE,{"disambiguationData":[OSD([sQuery(id+"F2.wireOp",EDGE,"E5.3.19.0")])]})});
            var Q208;
            {var subQ0=sQuery(id+"F0.wireOp",EDGE,"E1");Q208=makeQuery(id+"F3.boolean.opBoolean","SPLIT",FACE,{"disambiguationData":[TD([makeQuery(id+"F3.opExtrude","SWEPT_FACE",FACE,{"disambiguationData":[OSD([sQuery(id+"F2.wireOp",EDGE,"E3.10.0.2")])]})])],"derivedFrom":makeQuery(id+"F1.opExtrude","SWEPT_FACE",FACE,{"disambiguationData":[OSD([subQ0])]})});}
            var Q209;
            Q209=makeQuery(id+"F3.boolean.opBoolean","COPY",EDGE,{"derivedFrom":makeQuery(id+"F3.opExtrude","SWEPT_EDGE",EDGE,{"disambiguationData":[OSD([sQuery(id+"F2.wireOp",EDGE,"E3.13.0.1"),sQuery(id+"F2.wireOp",EDGE,"E3.13.0.2")])]})});
            var Q210;
            Q210=makeQuery(id+"F3.boolean.opBoolean","COPY",EDGE,{"derivedFrom":makeQuery(id+"F3.opExtrude","SWEPT_EDGE",EDGE,{"disambiguationData":[OSD([sQuery(id+"F0.wireOp",EDGE,"E1"),sQuery(id+"F2.wireOp",EDGE,"E3.1.0.2")])]})});
            var Q211;
            Q211=makeQuery(id+"F3.boolean.opBoolean","INTERSECT",EDGE,{"derivedFrom":[makeQuery(id+"F1.opExtrude","CAP_FACE",FACE,{"disambiguationData":[OSD([sQuery(id+"F0.wireOp",EDGE,"E0"),sQuery(id+"F0.wireOp",EDGE,"E1")])],"isStart":true}),makeQuery(id+"F3.opExtrude","SWEPT_FACE",FACE,{"disambiguationData":[OSD([sQuery(id+"F2.wireOp",EDGE,"E3.5.0.0")])]})]});
            var Q212;
            Q212=makeQuery(id+"F3.boolean.opBoolean","INTERSECT",EDGE,{"derivedFrom":[makeQuery(id+"F1.opExtrude","CAP_FACE",FACE,{"disambiguationData":[OSD([sQuery(id+"F0.wireOp",EDGE,"E0"),sQuery(id+"F0.wireOp",EDGE,"E1")])],"isStart":true}),makeQuery(id+"F3.opExtrude","SWEPT_FACE",FACE,{"disambiguationData":[OSD([sQuery(id+"F2.wireOp",EDGE,"E4.6.15.0")])]})]});
            var Q213;
            {var subQ1=sQuery(id+"F0.wireOp",EDGE,"E1");Q213=makeQuery(id+"F3.boolean.opBoolean","SPLIT",EDGE,{"disambiguationData":[TD([makeQuery(id+"F3.opExtrude","SWEPT_FACE",FACE,{"disambiguationData":[OSD([sQuery(id+"F2.wireOp",EDGE,"E5.6.19.0")])]})])],"derivedFrom":makeQuery(id+"F1.opExtrude","CAP_EDGE",EDGE,{"disambiguationData":[OSD([subQ1])],"isStart":false})});}
            var Q214;
            {var subQ0=sQuery(id+"F0.wireOp",EDGE,"E1");Q214=makeQuery(id+"F3.boolean.opBoolean","SPLIT",EDGE,{"disambiguationData":[TD([makeQuery(id+"F3.opExtrude","SWEPT_FACE",FACE,{"disambiguationData":[OSD([sQuery(id+"F2.wireOp",EDGE,"E4.6.15.0")])]})])],"derivedFrom":makeQuery(id+"F1.opExtrude","CAP_EDGE",EDGE,{"disambiguationData":[OSD([subQ0])],"isStart":false})});}
            var Q215;
            {var subQ0=sQuery(id+"F0.wireOp",EDGE,"E1");Q215=makeQuery(id+"F3.boolean.opBoolean","SPLIT",EDGE,{"disambiguationData":[TD([makeQuery(id+"F3.opExtrude","SWEPT_FACE",FACE,{"disambiguationData":[OSD([sQuery(id+"F2.wireOp",EDGE,"E3.12.0.2")])]})])],"derivedFrom":makeQuery(id+"F1.opExtrude","CAP_EDGE",EDGE,{"disambiguationData":[OSD([subQ0])],"isStart":true})});}
            var Q216;
            Q216=makeQuery(id+"F3.boolean.opBoolean","COPY",FACE,{"derivedFrom":makeQuery(id+"F3.opExtrude","SWEPT_FACE",FACE,{"disambiguationData":[OSD([sQuery(id+"F2.wireOp",EDGE,"E3.9.0.0")])]})});
            var Q217;
            Q217=makeQuery(id+"F3.boolean.opBoolean","COPY",FACE,{"derivedFrom":makeQuery(id+"F3.opExtrude","SWEPT_FACE",FACE,{"disambiguationData":[OSD([sQuery(id+"F2.wireOp",EDGE,"E3.14.0.1")])]})});
            var Q218;
            {var subQ0=sQuery(id+"F0.wireOp",EDGE,"E1");Q218=makeQuery(id+"F3.boolean.opBoolean","SPLIT",FACE,{"disambiguationData":[TD([makeQuery(id+"F3.opExtrude","SWEPT_FACE",FACE,{"disambiguationData":[OSD([sQuery(id+"F2.wireOp",EDGE,"E3.11.0.2")])]})])],"derivedFrom":makeQuery(id+"F1.opExtrude","SWEPT_FACE",FACE,{"disambiguationData":[OSD([subQ0])]})});}
            var Q219;
            Q219=makeQuery(id+"F3.boolean.opBoolean","COPY",EDGE,{"derivedFrom":makeQuery(id+"F3.opExtrude","SWEPT_EDGE",EDGE,{"disambiguationData":[OSD([sQuery(id+"F0.wireOp",EDGE,"E1"),sQuery(id+"F2.wireOp",EDGE,"E3.2.0.0")])]})});
            var Q220;
            Q220=makeQuery(id+"F3.boolean.opBoolean","COPY",EDGE,{"derivedFrom":makeQuery(id+"F3.opExtrude","CAP_EDGE",EDGE,{"disambiguationData":[OSD([sQuery(id+"F2.wireOp",EDGE,"E3.14.0.2")])],"isStart":true})});
            var Q221;
            Q221=makeQuery(id+"F3.boolean.opBoolean","INTERSECT",EDGE,{"derivedFrom":[makeQuery(id+"F1.opExtrude","CAP_FACE",FACE,{"disambiguationData":[OSD([sQuery(id+"F0.wireOp",EDGE,"E0"),sQuery(id+"F0.wireOp",EDGE,"E1")])],"isStart":true}),makeQuery(id+"F3.opExtrude","SWEPT_FACE",FACE,{"disambiguationData":[OSD([sQuery(id+"F2.wireOp",EDGE,"E3.10.0.2")])]})]});
            var Q222;
            Q222=makeQuery(id+"F3.boolean.opBoolean","INTERSECT",EDGE,{"derivedFrom":[makeQuery(id+"F1.opExtrude","CAP_FACE",FACE,{"disambiguationData":[OSD([sQuery(id+"F0.wireOp",EDGE,"E0"),sQuery(id+"F0.wireOp",EDGE,"E1")])],"isStart":true}),makeQuery(id+"F3.opExtrude","SWEPT_FACE",FACE,{"disambiguationData":[OSD([sQuery(id+"F2.wireOp",EDGE,"E4.0.16.0")])]})]});
            var Q223;
            {var subQ0=sQuery(id+"F0.wireOp",EDGE,"E1");Q223=makeQuery(id+"F3.boolean.opBoolean","SPLIT",EDGE,{"disambiguationData":[TD([makeQuery(id+"F3.opExtrude","SWEPT_FACE",FACE,{"disambiguationData":[OSD([sQuery(id+"F2.wireOp",EDGE,"E2.right")])]})])],"derivedFrom":makeQuery(id+"F1.opExtrude","CAP_EDGE",EDGE,{"disambiguationData":[OSD([subQ0])],"isStart":false})});}
            var Q224;
            {var subQ0=sQuery(id+"F0.wireOp",EDGE,"E1");Q224=makeQuery(id+"F3.boolean.opBoolean","SPLIT",EDGE,{"disambiguationData":[TD([makeQuery(id+"F3.opExtrude","SWEPT_FACE",FACE,{"disambiguationData":[OSD([sQuery(id+"F2.wireOp",EDGE,"E4.6.16.0")])]})])],"derivedFrom":makeQuery(id+"F1.opExtrude","CAP_EDGE",EDGE,{"disambiguationData":[OSD([subQ0])],"isStart":false})});}
            var Q225;
            {var subQ0=sQuery(id+"F0.wireOp",EDGE,"E1");Q225=makeQuery(id+"F3.boolean.opBoolean","SPLIT",EDGE,{"disambiguationData":[TD([makeQuery(id+"F3.opExtrude","SWEPT_FACE",FACE,{"disambiguationData":[OSD([sQuery(id+"F2.wireOp",EDGE,"E3.13.0.2")])]})])],"derivedFrom":makeQuery(id+"F1.opExtrude","CAP_EDGE",EDGE,{"disambiguationData":[OSD([subQ0])],"isStart":true})});}
            var Q226;
            Q226=makeQuery(id+"F3.boolean.opBoolean","COPY",FACE,{"derivedFrom":makeQuery(id+"F3.opExtrude","SWEPT_FACE",FACE,{"disambiguationData":[OSD([sQuery(id+"F2.wireOp",EDGE,"E3.9.0.1")])]})});
            var Q227;
            {var subQ0=sQuery(id+"F0.wireOp",EDGE,"E1");Q227=makeQuery(id+"F3.boolean.opBoolean","SPLIT",FACE,{"disambiguationData":[TD([makeQuery(id+"F3.opExtrude","SWEPT_FACE",FACE,{"disambiguationData":[OSD([sQuery(id+"F2.wireOp",EDGE,"E3.12.0.2")])]})])],"derivedFrom":makeQuery(id+"F1.opExtrude","SWEPT_FACE",FACE,{"disambiguationData":[OSD([subQ0])]})});}
            var Q228;
            Q228=makeQuery(id+"F3.boolean.opBoolean","COPY",EDGE,{"derivedFrom":makeQuery(id+"F3.opExtrude","SWEPT_EDGE",EDGE,{"disambiguationData":[OSD([sQuery(id+"F2.wireOp",EDGE,"E3.7.0.0"),sQuery(id+"F2.wireOp",EDGE,"E3.7.0.1")])]})});
            var Q229;
            Q229=makeQuery(id+"F3.boolean.opBoolean","COPY",EDGE,{"derivedFrom":makeQuery(id+"F3.opExtrude","SWEPT_EDGE",EDGE,{"disambiguationData":[OSD([sQuery(id+"F2.wireOp",EDGE,"E2.bottom"),sQuery(id+"F2.wireOp",EDGE,"E2.left")])]})});
            var Q230;
            Q230=makeQuery(id+"F3.boolean.opBoolean","COPY",EDGE,{"derivedFrom":makeQuery(id+"F3.opExtrude","SWEPT_EDGE",EDGE,{"disambiguationData":[OSD([sQuery(id+"F2.wireOp",EDGE,"E3.1.0.0"),sQuery(id+"F2.wireOp",EDGE,"E3.1.0.1")])]})});
            var Q231;
            Q231=makeQuery(id+"F3.boolean.opBoolean","COPY",EDGE,{"derivedFrom":makeQuery(id+"F3.opExtrude","SWEPT_EDGE",EDGE,{"disambiguationData":[OSD([sQuery(id+"F2.wireOp",EDGE,"E3.2.0.0"),sQuery(id+"F2.wireOp",EDGE,"E3.2.0.1")])]})});
            var Q232;
            Q232=makeQuery(id+"F3.boolean.opBoolean","COPY",EDGE,{"derivedFrom":makeQuery(id+"F3.opExtrude","SWEPT_EDGE",EDGE,{"disambiguationData":[OSD([sQuery(id+"F2.wireOp",EDGE,"E3.3.0.0"),sQuery(id+"F2.wireOp",EDGE,"E3.3.0.1")])]})});
            var Q233;
            Q233=makeQuery(id+"F3.boolean.opBoolean","COPY",EDGE,{"derivedFrom":makeQuery(id+"F3.opExtrude","SWEPT_EDGE",EDGE,{"disambiguationData":[OSD([sQuery(id+"F2.wireOp",EDGE,"E3.4.0.0"),sQuery(id+"F2.wireOp",EDGE,"E3.4.0.1")])]})});
            var Q234;
            Q234=makeQuery(id+"F3.boolean.opBoolean","COPY",EDGE,{"derivedFrom":makeQuery(id+"F3.opExtrude","SWEPT_EDGE",EDGE,{"disambiguationData":[OSD([sQuery(id+"F2.wireOp",EDGE,"E3.5.0.0"),sQuery(id+"F2.wireOp",EDGE,"E3.5.0.1")])]})});
            var Q235;
            Q235=makeQuery(id+"F3.boolean.opBoolean","COPY",EDGE,{"derivedFrom":makeQuery(id+"F3.opExtrude","SWEPT_EDGE",EDGE,{"disambiguationData":[OSD([sQuery(id+"F2.wireOp",EDGE,"E3.6.0.0"),sQuery(id+"F2.wireOp",EDGE,"E3.6.0.1")])]})});
            var Q236;
            Q236=makeQuery(id+"F3.boolean.opBoolean","COPY",EDGE,{"derivedFrom":makeQuery(id+"F3.opExtrude","SWEPT_EDGE",EDGE,{"disambiguationData":[OSD([sQuery(id+"F2.wireOp",EDGE,"E3.14.0.1"),sQuery(id+"F2.wireOp",EDGE,"E3.14.0.2")])]})});
            var Q237;
            Q237=makeQuery(id+"F3.boolean.opBoolean","COPY",EDGE,{"derivedFrom":makeQuery(id+"F3.opExtrude","SWEPT_EDGE",EDGE,{"disambiguationData":[OSD([sQuery(id+"F0.wireOp",EDGE,"E1"),sQuery(id+"F2.wireOp",EDGE,"E3.2.0.2")])]})});
            var Q238;
            Q238=makeQuery(id+"F3.boolean.opBoolean","COPY",EDGE,{"derivedFrom":makeQuery(id+"F3.opExtrude","SWEPT_EDGE",EDGE,{"disambiguationData":[OSD([sQuery(id+"F0.wireOp",EDGE,"E1"),sQuery(id+"F2.wireOp",EDGE,"E3.10.0.2")])]})});
            var Q239;
            Q239=makeQuery(id+"F3.boolean.opBoolean","COPY",EDGE,{"derivedFrom":makeQuery(id+"F3.opExtrude","SWEPT_EDGE",EDGE,{"disambiguationData":[OSD([sQuery(id+"F0.wireOp",EDGE,"E1"),sQuery(id+"F2.wireOp",EDGE,"E5.6.18.0")])]})});
            var Q240;
            Q240=makeQuery(id+"F3.boolean.opBoolean","COPY",EDGE,{"derivedFrom":makeQuery(id+"F3.opExtrude","CAP_EDGE",EDGE,{"disambiguationData":[OSD([sQuery(id+"F2.wireOp",EDGE,"E3.4.0.1")])],"isStart":true})});
            var Q241;
            Q241=makeQuery(id+"F3.boolean.opBoolean","INTERSECT",EDGE,{"derivedFrom":[makeQuery(id+"F1.opExtrude","CAP_FACE",FACE,{"disambiguationData":[OSD([sQuery(id+"F0.wireOp",EDGE,"E0"),sQuery(id+"F0.wireOp",EDGE,"E1")])],"isStart":true}),makeQuery(id+"F3.opExtrude","SWEPT_FACE",FACE,{"disambiguationData":[OSD([sQuery(id+"F2.wireOp",EDGE,"E4.3.16.0")])]})]});
            var Q242;
            Q242=makeQuery(id+"F3.boolean.opBoolean","COPY",EDGE,{"derivedFrom":makeQuery(id+"F3.opExtrude","SWEPT_EDGE",EDGE,{"disambiguationData":[OSD([sQuery(id+"F2.wireOp",EDGE,"E4.0.15.0"),sQuery(id+"F2.wireOp",EDGE,"E4.3.15.0")])]})});
            var Q243;
            Q243=makeQuery(id+"F3.boolean.opBoolean","COPY",EDGE,{"derivedFrom":makeQuery(id+"F3.opExtrude","SWEPT_EDGE",EDGE,{"disambiguationData":[OSD([sQuery(id+"F0.wireOp",EDGE,"E1"),sQuery(id+"F2.wireOp",EDGE,"E3.3.0.0")])]})});
            var Q244;
            Q244=makeQuery(id+"F3.boolean.opBoolean","COPY",EDGE,{"derivedFrom":makeQuery(id+"F3.opExtrude","SWEPT_EDGE",EDGE,{"disambiguationData":[OSD([sQuery(id+"F0.wireOp",EDGE,"E1"),sQuery(id+"F2.wireOp",EDGE,"E3.11.0.0")])]})});
            var Q245;
            Q245=makeQuery(id+"F3.boolean.opBoolean","COPY",EDGE,{"derivedFrom":makeQuery(id+"F3.opExtrude","SWEPT_EDGE",EDGE,{"disambiguationData":[OSD([sQuery(id+"F0.wireOp",EDGE,"E1"),sQuery(id+"F2.wireOp",EDGE,"E5.0.19.0")])]})});
            var Q246;
            Q246=makeQuery(id+"F3.boolean.opBoolean","COPY",EDGE,{"derivedFrom":makeQuery(id+"F3.opExtrude","CAP_EDGE",EDGE,{"disambiguationData":[OSD([sQuery(id+"F2.wireOp",EDGE,"E4.3.15.0")])],"isStart":true})});
            var Q247;
            Q247=makeQuery(id+"F3.boolean.opBoolean","INTERSECT",EDGE,{"derivedFrom":[makeQuery(id+"F1.opExtrude","CAP_FACE",FACE,{"disambiguationData":[OSD([sQuery(id+"F0.wireOp",EDGE,"E0"),sQuery(id+"F0.wireOp",EDGE,"E1")])],"isStart":true}),makeQuery(id+"F3.opExtrude","SWEPT_FACE",FACE,{"disambiguationData":[OSD([sQuery(id+"F2.wireOp",EDGE,"E3.11.0.1")])]})]});
            var Q248;
            Q248=makeQuery(id+"F3.boolean.opBoolean","COPY",EDGE,{"derivedFrom":makeQuery(id+"F3.opExtrude","SWEPT_EDGE",EDGE,{"disambiguationData":[OSD([sQuery(id+"F0.wireOp",EDGE,"E1"),sQuery(id+"F2.wireOp",EDGE,"E3.3.0.2")])]})});
            var Q249;
            Q249=makeQuery(id+"F3.boolean.opBoolean","COPY",EDGE,{"derivedFrom":makeQuery(id+"F3.opExtrude","SWEPT_EDGE",EDGE,{"disambiguationData":[OSD([sQuery(id+"F0.wireOp",EDGE,"E1"),sQuery(id+"F2.wireOp",EDGE,"E3.11.0.2")])]})});
            var Q250;
            Q250=makeQuery(id+"F3.boolean.opBoolean","COPY",EDGE,{"derivedFrom":makeQuery(id+"F3.opExtrude","CAP_EDGE",EDGE,{"disambiguationData":[OSD([sQuery(id+"F2.wireOp",EDGE,"E3.10.0.1")])],"isStart":true})});
            var Q251;
            Q251=makeQuery(id+"F3.boolean.opBoolean","INTERSECT",EDGE,{"derivedFrom":[makeQuery(id+"F1.opExtrude","CAP_FACE",FACE,{"disambiguationData":[OSD([sQuery(id+"F0.wireOp",EDGE,"E0"),sQuery(id+"F0.wireOp",EDGE,"E1")])],"isStart":true}),makeQuery(id+"F3.opExtrude","SWEPT_FACE",FACE,{"disambiguationData":[OSD([sQuery(id+"F2.wireOp",EDGE,"E3.6.0.1")])]})]});
            var Q252;
            Q252=makeQuery(id+"F3.boolean.opBoolean","COPY",EDGE,{"derivedFrom":makeQuery(id+"F3.opExtrude","SWEPT_EDGE",EDGE,{"disambiguationData":[OSD([sQuery(id+"F2.wireOp",EDGE,"E3.8.0.0"),sQuery(id+"F2.wireOp",EDGE,"E3.8.0.1")])]})});
            var Q253;
            Q253=makeQuery(id+"F3.boolean.opBoolean","COPY",EDGE,{"derivedFrom":makeQuery(id+"F3.opExtrude","SWEPT_EDGE",EDGE,{"disambiguationData":[OSD([sQuery(id+"F2.wireOp",EDGE,"E4.0.16.0"),sQuery(id+"F2.wireOp",EDGE,"E4.3.16.0")])]})});
            var Q254;
            Q254=makeQuery(id+"F3.boolean.opBoolean","COPY",EDGE,{"derivedFrom":makeQuery(id+"F3.opExtrude","SWEPT_EDGE",EDGE,{"disambiguationData":[OSD([sQuery(id+"F0.wireOp",EDGE,"E1"),sQuery(id+"F2.wireOp",EDGE,"E3.4.0.0")])]})});
            var Q255;
            Q255=makeQuery(id+"F3.boolean.opBoolean","COPY",EDGE,{"derivedFrom":makeQuery(id+"F3.opExtrude","SWEPT_EDGE",EDGE,{"disambiguationData":[OSD([sQuery(id+"F0.wireOp",EDGE,"E1"),sQuery(id+"F2.wireOp",EDGE,"E3.12.0.0")])]})});
            var Q256;
            Q256=makeQuery(id+"F3.boolean.opBoolean","COPY",EDGE,{"derivedFrom":makeQuery(id+"F3.opExtrude","CAP_EDGE",EDGE,{"disambiguationData":[OSD([sQuery(id+"F2.wireOp",EDGE,"E2.bottom")])],"isStart":true})});
            var Q257;
            Q257=makeQuery(id+"F3.boolean.opBoolean","COPY",EDGE,{"derivedFrom":makeQuery(id+"F3.opExtrude","CAP_EDGE",EDGE,{"disambiguationData":[OSD([sQuery(id+"F2.wireOp",EDGE,"E3.5.0.1")])],"isStart":true})});
            var Q258;
            Q258=makeQuery(id+"F3.boolean.opBoolean","INTERSECT",EDGE,{"derivedFrom":[makeQuery(id+"F1.opExtrude","CAP_FACE",FACE,{"disambiguationData":[OSD([sQuery(id+"F0.wireOp",EDGE,"E0"),sQuery(id+"F0.wireOp",EDGE,"E1")])],"isStart":true}),makeQuery(id+"F3.opExtrude","SWEPT_FACE",FACE,{"disambiguationData":[OSD([sQuery(id+"F2.wireOp",EDGE,"E3.1.0.1")])]})]});
            var Q259;
            Q259=makeQuery(id+"F3.boolean.opBoolean","INTERSECT",EDGE,{"derivedFrom":[makeQuery(id+"F1.opExtrude","CAP_FACE",FACE,{"disambiguationData":[OSD([sQuery(id+"F0.wireOp",EDGE,"E0"),sQuery(id+"F0.wireOp",EDGE,"E1")])],"isStart":true}),makeQuery(id+"F3.opExtrude","SWEPT_FACE",FACE,{"disambiguationData":[OSD([sQuery(id+"F2.wireOp",EDGE,"E4.3.17.0")])]})]});
            var Q260;
            Q260=makeQuery(id+"F3.boolean.opBoolean","COPY",EDGE,{"derivedFrom":makeQuery(id+"F3.opExtrude","SWEPT_EDGE",EDGE,{"disambiguationData":[OSD([sQuery(id+"F2.wireOp",EDGE,"E4.3.16.0"),sQuery(id+"F2.wireOp",EDGE,"E4.6.16.0")])]})});
            var Q261;
            Q261=makeQuery(id+"F3.boolean.opBoolean","COPY",EDGE,{"derivedFrom":makeQuery(id+"F3.opExtrude","SWEPT_EDGE",EDGE,{"disambiguationData":[OSD([sQuery(id+"F0.wireOp",EDGE,"E1"),sQuery(id+"F2.wireOp",EDGE,"E3.4.0.2")])]})});
            var Q262;
            Q262=makeQuery(id+"F3.boolean.opBoolean","COPY",EDGE,{"derivedFrom":makeQuery(id+"F3.opExtrude","SWEPT_EDGE",EDGE,{"disambiguationData":[OSD([sQuery(id+"F0.wireOp",EDGE,"E1"),sQuery(id+"F2.wireOp",EDGE,"E3.12.0.2")])]})});
            var Q263;
            Q263=makeQuery(id+"F3.boolean.opBoolean","INTERSECT",EDGE,{"derivedFrom":[makeQuery(id+"F1.opExtrude","CAP_FACE",FACE,{"disambiguationData":[OSD([sQuery(id+"F0.wireOp",EDGE,"E0"),sQuery(id+"F0.wireOp",EDGE,"E1")])],"isStart":true}),makeQuery(id+"F3.opExtrude","SWEPT_FACE",FACE,{"disambiguationData":[OSD([sQuery(id+"F2.wireOp",EDGE,"E3.12.0.1")])]})]});
            var Q264;
            Q264=makeQuery(id+"F3.boolean.opBoolean","COPY",EDGE,{"derivedFrom":makeQuery(id+"F3.opExtrude","SWEPT_EDGE",EDGE,{"disambiguationData":[OSD([sQuery(id+"F2.wireOp",EDGE,"E3.9.0.0"),sQuery(id+"F2.wireOp",EDGE,"E3.9.0.1")])]})});
            var Q265;
            Q265=makeQuery(id+"F3.boolean.opBoolean","COPY",EDGE,{"derivedFrom":makeQuery(id+"F3.opExtrude","SWEPT_EDGE",EDGE,{"disambiguationData":[OSD([sQuery(id+"F2.wireOp",EDGE,"E4.0.17.0"),sQuery(id+"F2.wireOp",EDGE,"E4.3.17.0")])]})});
            var Q266;
            Q266=makeQuery(id+"F3.boolean.opBoolean","COPY",EDGE,{"derivedFrom":makeQuery(id+"F3.opExtrude","SWEPT_EDGE",EDGE,{"disambiguationData":[OSD([sQuery(id+"F0.wireOp",EDGE,"E1"),sQuery(id+"F2.wireOp",EDGE,"E3.5.0.0")])]})});
            var Q267;
            Q267=makeQuery(id+"F3.boolean.opBoolean","COPY",EDGE,{"derivedFrom":makeQuery(id+"F3.opExtrude","SWEPT_EDGE",EDGE,{"disambiguationData":[OSD([sQuery(id+"F0.wireOp",EDGE,"E1"),sQuery(id+"F2.wireOp",EDGE,"E3.13.0.0")])]})});
            var Q268;
            Q268=makeQuery(id+"F3.boolean.opBoolean","COPY",EDGE,{"derivedFrom":makeQuery(id+"F3.opExtrude","CAP_EDGE",EDGE,{"disambiguationData":[OSD([sQuery(id+"F2.wireOp",EDGE,"E3.11.0.1")])],"isStart":true})});
            var Q269;
            Q269=makeQuery(id+"F3.boolean.opBoolean","INTERSECT",EDGE,{"derivedFrom":[makeQuery(id+"F1.opExtrude","CAP_FACE",FACE,{"disambiguationData":[OSD([sQuery(id+"F0.wireOp",EDGE,"E0"),sQuery(id+"F0.wireOp",EDGE,"E1")])],"isStart":true}),makeQuery(id+"F3.opExtrude","SWEPT_FACE",FACE,{"disambiguationData":[OSD([sQuery(id+"F2.wireOp",EDGE,"E3.7.0.1")])]})]});
            var Q270;
            Q270=makeQuery(id+"F3.boolean.opBoolean","INTERSECT",EDGE,{"derivedFrom":[makeQuery(id+"F1.opExtrude","CAP_FACE",FACE,{"disambiguationData":[OSD([sQuery(id+"F0.wireOp",EDGE,"E0"),sQuery(id+"F0.wireOp",EDGE,"E1")])],"isStart":true}),makeQuery(id+"F3.opExtrude","SWEPT_FACE",FACE,{"disambiguationData":[OSD([sQuery(id+"F2.wireOp",EDGE,"E5.0.18.0")])]})]});
            var Q271;
            Q271=makeQuery(id+"F3.boolean.opBoolean","COPY",EDGE,{"derivedFrom":makeQuery(id+"F3.opExtrude","SWEPT_EDGE",EDGE,{"disambiguationData":[OSD([sQuery(id+"F0.wireOp",EDGE,"E1"),sQuery(id+"F2.wireOp",EDGE,"E3.5.0.2")])]})});
            var Q272;
            Q272=makeQuery(id+"F3.boolean.opBoolean","COPY",EDGE,{"derivedFrom":makeQuery(id+"F3.opExtrude","SWEPT_EDGE",EDGE,{"disambiguationData":[OSD([sQuery(id+"F0.wireOp",EDGE,"E1"),sQuery(id+"F2.wireOp",EDGE,"E3.13.0.2")])]})});
            var Q273;
            Q273=makeQuery(id+"F3.boolean.opBoolean","COPY",EDGE,{"derivedFrom":makeQuery(id+"F3.opExtrude","CAP_EDGE",EDGE,{"disambiguationData":[OSD([sQuery(id+"F2.wireOp",EDGE,"E3.6.0.1")])],"isStart":true})});
            var Q274;
            Q274=makeQuery(id+"F3.boolean.opBoolean","INTERSECT",EDGE,{"derivedFrom":[makeQuery(id+"F1.opExtrude","CAP_FACE",FACE,{"disambiguationData":[OSD([sQuery(id+"F0.wireOp",EDGE,"E0"),sQuery(id+"F0.wireOp",EDGE,"E1")])],"isStart":true}),makeQuery(id+"F3.opExtrude","SWEPT_FACE",FACE,{"disambiguationData":[OSD([sQuery(id+"F2.wireOp",EDGE,"E3.2.0.1")])]})]});
            var Q275;
            Q275=makeQuery(id+"F3.boolean.opBoolean","INTERSECT",EDGE,{"derivedFrom":[makeQuery(id+"F1.opExtrude","CAP_FACE",FACE,{"disambiguationData":[OSD([sQuery(id+"F0.wireOp",EDGE,"E0"),sQuery(id+"F0.wireOp",EDGE,"E1")])],"isStart":true}),makeQuery(id+"F3.opExtrude","SWEPT_FACE",FACE,{"disambiguationData":[OSD([sQuery(id+"F2.wireOp",EDGE,"E5.3.18.0")])]})]});
            var Q276;
            Q276=makeQuery(id+"F3.boolean.opBoolean","COPY",EDGE,{"derivedFrom":makeQuery(id+"F3.opExtrude","SWEPT_EDGE",EDGE,{"disambiguationData":[OSD([sQuery(id+"F2.wireOp",EDGE,"E3.10.0.0"),sQuery(id+"F2.wireOp",EDGE,"E3.10.0.1")])]})});
            var Q277;
            Q277=makeQuery(id+"F3.boolean.opBoolean","COPY",EDGE,{"derivedFrom":makeQuery(id+"F3.opExtrude","SWEPT_EDGE",EDGE,{"disambiguationData":[OSD([sQuery(id+"F2.wireOp",EDGE,"E5.0.18.0"),sQuery(id+"F2.wireOp",EDGE,"E5.3.18.0")])]})});
            var Q278;
            Q278=makeQuery(id+"F3.boolean.opBoolean","COPY",EDGE,{"derivedFrom":makeQuery(id+"F3.opExtrude","SWEPT_EDGE",EDGE,{"disambiguationData":[OSD([sQuery(id+"F0.wireOp",EDGE,"E1"),sQuery(id+"F2.wireOp",EDGE,"E3.6.0.0")])]})});
            var Q279;
            Q279=makeQuery(id+"F3.boolean.opBoolean","COPY",EDGE,{"derivedFrom":makeQuery(id+"F3.opExtrude","SWEPT_EDGE",EDGE,{"disambiguationData":[OSD([sQuery(id+"F0.wireOp",EDGE,"E1"),sQuery(id+"F2.wireOp",EDGE,"E3.14.0.0")])]})});
            var Q280;
            Q280=makeQuery(id+"F3.boolean.opBoolean","COPY",EDGE,{"derivedFrom":makeQuery(id+"F3.opExtrude","CAP_EDGE",EDGE,{"disambiguationData":[OSD([sQuery(id+"F2.wireOp",EDGE,"E3.1.0.1")])],"isStart":true})});
            var Q281;
            Q281=makeQuery(id+"F3.boolean.opBoolean","COPY",EDGE,{"derivedFrom":makeQuery(id+"F3.opExtrude","CAP_EDGE",EDGE,{"disambiguationData":[OSD([sQuery(id+"F2.wireOp",EDGE,"E4.3.17.0")])],"isStart":true})});
            var Q282;
            Q282=makeQuery(id+"F3.boolean.opBoolean","INTERSECT",EDGE,{"derivedFrom":[makeQuery(id+"F1.opExtrude","CAP_FACE",FACE,{"disambiguationData":[OSD([sQuery(id+"F0.wireOp",EDGE,"E0"),sQuery(id+"F0.wireOp",EDGE,"E1")])],"isStart":true}),makeQuery(id+"F3.opExtrude","SWEPT_FACE",FACE,{"disambiguationData":[OSD([sQuery(id+"F2.wireOp",EDGE,"E3.8.0.0")])]})]});
            var Q283;
            Q283=makeQuery(id+"F3.boolean.opBoolean","INTERSECT",EDGE,{"derivedFrom":[makeQuery(id+"F1.opExtrude","CAP_FACE",FACE,{"disambiguationData":[OSD([sQuery(id+"F0.wireOp",EDGE,"E0"),sQuery(id+"F0.wireOp",EDGE,"E1")])],"isStart":true}),makeQuery(id+"F3.opExtrude","SWEPT_FACE",FACE,{"disambiguationData":[OSD([sQuery(id+"F2.wireOp",EDGE,"E3.13.0.1")])]})]});
            var Q284;
            Q284=makeQuery(id+"F3.boolean.opBoolean","INTERSECT",EDGE,{"derivedFrom":[makeQuery(id+"F1.opExtrude","CAP_FACE",FACE,{"disambiguationData":[OSD([sQuery(id+"F0.wireOp",EDGE,"E0"),sQuery(id+"F0.wireOp",EDGE,"E1")])],"isStart":true}),makeQuery(id+"F3.opExtrude","SWEPT_FACE",FACE,{"disambiguationData":[OSD([sQuery(id+"F2.wireOp",EDGE,"E5.6.18.0")])]})]});
            var Q285;
            Q285=makeQuery(id+"F3.boolean.opBoolean","COPY",EDGE,{"derivedFrom":makeQuery(id+"F3.opExtrude","SWEPT_EDGE",EDGE,{"disambiguationData":[OSD([sQuery(id+"F2.wireOp",EDGE,"E5.3.18.0"),sQuery(id+"F2.wireOp",EDGE,"E5.6.18.0")])]})});
            var Q286;
            Q286=makeQuery(id+"F3.boolean.opBoolean","COPY",EDGE,{"derivedFrom":makeQuery(id+"F3.opExtrude","SWEPT_EDGE",EDGE,{"disambiguationData":[OSD([sQuery(id+"F0.wireOp",EDGE,"E1"),sQuery(id+"F2.wireOp",EDGE,"E3.6.0.2")])]})});
            var Q287;
            Q287=makeQuery(id+"F3.boolean.opBoolean","COPY",EDGE,{"derivedFrom":makeQuery(id+"F3.opExtrude","SWEPT_EDGE",EDGE,{"disambiguationData":[OSD([sQuery(id+"F0.wireOp",EDGE,"E1"),sQuery(id+"F2.wireOp",EDGE,"E3.14.0.2")])]})});
            var Q288;
            Q288=makeQuery(id+"F3.boolean.opBoolean","COPY",EDGE,{"derivedFrom":makeQuery(id+"F3.opExtrude","CAP_EDGE",EDGE,{"disambiguationData":[OSD([sQuery(id+"F2.wireOp",EDGE,"E3.12.0.1")])],"isStart":true})});
            var Q289;
            Q289=makeQuery(id+"F3.boolean.opBoolean","INTERSECT",EDGE,{"derivedFrom":[makeQuery(id+"F1.opExtrude","CAP_FACE",FACE,{"disambiguationData":[OSD([sQuery(id+"F0.wireOp",EDGE,"E0"),sQuery(id+"F0.wireOp",EDGE,"E1")])],"isStart":true}),makeQuery(id+"F3.opExtrude","SWEPT_FACE",FACE,{"disambiguationData":[OSD([sQuery(id+"F2.wireOp",EDGE,"E3.8.0.1")])]})]});
            var Q290;
            Q290=makeQuery(id+"F3.boolean.opBoolean","COPY",EDGE,{"derivedFrom":makeQuery(id+"F3.opExtrude","SWEPT_EDGE",EDGE,{"disambiguationData":[OSD([sQuery(id+"F2.wireOp",EDGE,"E3.11.0.0"),sQuery(id+"F2.wireOp",EDGE,"E3.11.0.1")])]})});
            var Q291;
            Q291=makeQuery(id+"F3.boolean.opBoolean","COPY",EDGE,{"derivedFrom":makeQuery(id+"F3.opExtrude","SWEPT_EDGE",EDGE,{"disambiguationData":[OSD([sQuery(id+"F2.wireOp",EDGE,"E5.0.19.0"),sQuery(id+"F2.wireOp",EDGE,"E5.3.19.0")])]})});
            var Q292;
            Q292=makeQuery(id+"F3.boolean.opBoolean","COPY",EDGE,{"derivedFrom":makeQuery(id+"F3.opExtrude","SWEPT_EDGE",EDGE,{"disambiguationData":[OSD([sQuery(id+"F0.wireOp",EDGE,"E1"),sQuery(id+"F2.wireOp",EDGE,"E3.7.0.0")])]})});
            var Q293;
            Q293=makeQuery(id+"F3.boolean.opBoolean","COPY",EDGE,{"derivedFrom":makeQuery(id+"F3.opExtrude","SWEPT_EDGE",EDGE,{"disambiguationData":[OSD([sQuery(id+"F0.wireOp",EDGE,"E1"),sQuery(id+"F2.wireOp",EDGE,"E4.0.15.0")])]})});
            var Q294;
            Q294=makeQuery(id+"F3.boolean.opBoolean","COPY",EDGE,{"derivedFrom":makeQuery(id+"F3.opExtrude","CAP_EDGE",EDGE,{"disambiguationData":[OSD([sQuery(id+"F2.wireOp",EDGE,"E3.7.0.1")])],"isStart":true})});
            var Q295;
            Q295=makeQuery(id+"F3.boolean.opBoolean","INTERSECT",EDGE,{"derivedFrom":[makeQuery(id+"F1.opExtrude","CAP_FACE",FACE,{"disambiguationData":[OSD([sQuery(id+"F0.wireOp",EDGE,"E0"),sQuery(id+"F0.wireOp",EDGE,"E1")])],"isStart":true}),makeQuery(id+"F3.opExtrude","SWEPT_FACE",FACE,{"disambiguationData":[OSD([sQuery(id+"F2.wireOp",EDGE,"E3.3.0.1")])]})]});
            var Q296;
            Q296=makeQuery(id+"F3.boolean.opBoolean","INTERSECT",EDGE,{"derivedFrom":[makeQuery(id+"F1.opExtrude","CAP_FACE",FACE,{"disambiguationData":[OSD([sQuery(id+"F0.wireOp",EDGE,"E0"),sQuery(id+"F0.wireOp",EDGE,"E1")])],"isStart":true}),makeQuery(id+"F3.opExtrude","SWEPT_FACE",FACE,{"disambiguationData":[OSD([sQuery(id+"F2.wireOp",EDGE,"E5.3.19.0")])]})]});
            var Q297;
            Q297=makeQuery(id+"F3.boolean.opBoolean","COPY",EDGE,{"derivedFrom":makeQuery(id+"F3.opExtrude","SWEPT_EDGE",EDGE,{"disambiguationData":[OSD([sQuery(id+"F0.wireOp",EDGE,"E1"),sQuery(id+"F2.wireOp",EDGE,"E3.7.0.2")])]})});
            var Q298;
            Q298=makeQuery(id+"F3.boolean.opBoolean","COPY",EDGE,{"derivedFrom":makeQuery(id+"F3.opExtrude","SWEPT_EDGE",EDGE,{"disambiguationData":[OSD([sQuery(id+"F0.wireOp",EDGE,"E1"),sQuery(id+"F2.wireOp",EDGE,"E4.6.15.0")])]})});
            var Q299;
            Q299=makeQuery(id+"F3.boolean.opBoolean","COPY",EDGE,{"derivedFrom":makeQuery(id+"F3.opExtrude","CAP_EDGE",EDGE,{"disambiguationData":[OSD([sQuery(id+"F2.wireOp",EDGE,"E3.2.0.1")])],"isStart":true})});
            var Q300;
            Q300=makeQuery(id+"F3.boolean.opBoolean","INTERSECT",EDGE,{"derivedFrom":[makeQuery(id+"F1.opExtrude","CAP_FACE",FACE,{"disambiguationData":[OSD([sQuery(id+"F0.wireOp",EDGE,"E0"),sQuery(id+"F0.wireOp",EDGE,"E1")])],"isStart":true}),makeQuery(id+"F3.opExtrude","SWEPT_FACE",FACE,{"disambiguationData":[OSD([sQuery(id+"F2.wireOp",EDGE,"E3.14.0.1")])]})]});
            var Q301;
            Q301=makeQuery(id+"F3.boolean.opBoolean","COPY",EDGE,{"derivedFrom":makeQuery(id+"F3.opExtrude","SWEPT_EDGE",EDGE,{"disambiguationData":[OSD([sQuery(id+"F2.wireOp",EDGE,"E3.12.0.0"),sQuery(id+"F2.wireOp",EDGE,"E3.12.0.1")])]})});
            var Q302;
            Q302=makeQuery(id+"F3.boolean.opBoolean","COPY",EDGE,{"derivedFrom":makeQuery(id+"F3.opExtrude","SWEPT_EDGE",EDGE,{"disambiguationData":[OSD([sQuery(id+"F0.wireOp",EDGE,"E1"),sQuery(id+"F2.wireOp",EDGE,"E3.8.0.0")])]})});
            var Q303;
            Q303=makeQuery(id+"F3.boolean.opBoolean","COPY",EDGE,{"derivedFrom":makeQuery(id+"F3.opExtrude","SWEPT_EDGE",EDGE,{"disambiguationData":[OSD([sQuery(id+"F0.wireOp",EDGE,"E1"),sQuery(id+"F2.wireOp",EDGE,"E4.0.16.0")])]})});
            var Q304;
            Q304=makeQuery(id+"F3.boolean.opBoolean","COPY",EDGE,{"derivedFrom":makeQuery(id+"F3.opExtrude","CAP_EDGE",EDGE,{"disambiguationData":[OSD([sQuery(id+"F2.wireOp",EDGE,"E3.13.0.1")])],"isStart":true})});
            var Q305;
            Q305=makeQuery(id+"F3.boolean.opBoolean","INTERSECT",EDGE,{"derivedFrom":[makeQuery(id+"F1.opExtrude","CAP_FACE",FACE,{"disambiguationData":[OSD([sQuery(id+"F0.wireOp",EDGE,"E0"),sQuery(id+"F0.wireOp",EDGE,"E1")])],"isStart":true}),makeQuery(id+"F3.opExtrude","SWEPT_FACE",FACE,{"disambiguationData":[OSD([sQuery(id+"F2.wireOp",EDGE,"E3.9.0.1")])]})]});
            var Q306;
            Q306=makeQuery(id+"F3.boolean.opBoolean","COPY",EDGE,{"derivedFrom":makeQuery(id+"F3.opExtrude","SWEPT_EDGE",EDGE,{"disambiguationData":[OSD([sQuery(id+"F0.wireOp",EDGE,"E1"),sQuery(id+"F2.wireOp",EDGE,"E2.right")])]})});
            var Q307;
            Q307=makeQuery(id+"F3.boolean.opBoolean","COPY",EDGE,{"derivedFrom":makeQuery(id+"F3.opExtrude","SWEPT_EDGE",EDGE,{"disambiguationData":[OSD([sQuery(id+"F0.wireOp",EDGE,"E1"),sQuery(id+"F2.wireOp",EDGE,"E3.8.0.2")])]})});
            var Q308;
            Q308=makeQuery(id+"F3.boolean.opBoolean","COPY",EDGE,{"derivedFrom":makeQuery(id+"F3.opExtrude","SWEPT_EDGE",EDGE,{"disambiguationData":[OSD([sQuery(id+"F0.wireOp",EDGE,"E1"),sQuery(id+"F2.wireOp",EDGE,"E4.6.16.0")])]})});
            var Q309;
            Q309=makeQuery(id+"F3.boolean.opBoolean","COPY",EDGE,{"derivedFrom":makeQuery(id+"F3.opExtrude","CAP_EDGE",EDGE,{"disambiguationData":[OSD([sQuery(id+"F2.wireOp",EDGE,"E3.8.0.1")])],"isStart":true})});
            var Q310;
            Q310=makeQuery(id+"F3.boolean.opBoolean","INTERSECT",EDGE,{"derivedFrom":[makeQuery(id+"F1.opExtrude","CAP_FACE",FACE,{"disambiguationData":[OSD([sQuery(id+"F0.wireOp",EDGE,"E0"),sQuery(id+"F0.wireOp",EDGE,"E1")])],"isStart":true}),makeQuery(id+"F3.opExtrude","SWEPT_FACE",FACE,{"disambiguationData":[OSD([sQuery(id+"F2.wireOp",EDGE,"E3.4.0.1")])]})]});
            var Q311;
            Q311=makeQuery(id+"F3.boolean.opBoolean","COPY",EDGE,{"derivedFrom":makeQuery(id+"F3.opExtrude","SWEPT_EDGE",EDGE,{"disambiguationData":[OSD([sQuery(id+"F2.wireOp",EDGE,"E3.13.0.0"),sQuery(id+"F2.wireOp",EDGE,"E3.13.0.1")])]})});
            var Q312;
            Q312=makeQuery(id+"F3.boolean.opBoolean","COPY",EDGE,{"derivedFrom":makeQuery(id+"F3.opExtrude","SWEPT_EDGE",EDGE,{"disambiguationData":[OSD([sQuery(id+"F0.wireOp",EDGE,"E1"),sQuery(id+"F2.wireOp",EDGE,"E3.1.0.0")])]})});
            var Q313;
            Q313=makeQuery(id+"F3.boolean.opBoolean","COPY",EDGE,{"derivedFrom":makeQuery(id+"F3.opExtrude","SWEPT_EDGE",EDGE,{"disambiguationData":[OSD([sQuery(id+"F0.wireOp",EDGE,"E1"),sQuery(id+"F2.wireOp",EDGE,"E3.9.0.0")])]})});
            var Q314;
            Q314=makeQuery(id+"F3.boolean.opBoolean","COPY",EDGE,{"derivedFrom":makeQuery(id+"F3.opExtrude","SWEPT_EDGE",EDGE,{"disambiguationData":[OSD([sQuery(id+"F0.wireOp",EDGE,"E1"),sQuery(id+"F2.wireOp",EDGE,"E4.0.17.0")])]})});
            var Q315;
            Q315=makeQuery(id+"F3.boolean.opBoolean","COPY",EDGE,{"derivedFrom":makeQuery(id+"F3.opExtrude","CAP_EDGE",EDGE,{"disambiguationData":[OSD([sQuery(id+"F2.wireOp",EDGE,"E3.3.0.1")])],"isStart":true})});
            var Q316;
            Q316=makeQuery(id+"F3.boolean.opBoolean","COPY",EDGE,{"derivedFrom":makeQuery(id+"F3.opExtrude","CAP_EDGE",EDGE,{"disambiguationData":[OSD([sQuery(id+"F2.wireOp",EDGE,"E5.3.19.0")])],"isStart":true})});
            var Q317;
            Q317=makeQuery(id+"F3.boolean.opBoolean","INTERSECT",EDGE,{"derivedFrom":[makeQuery(id+"F1.opExtrude","CAP_FACE",FACE,{"disambiguationData":[OSD([sQuery(id+"F0.wireOp",EDGE,"E0"),sQuery(id+"F0.wireOp",EDGE,"E1")])],"isStart":true}),makeQuery(id+"F3.opExtrude","SWEPT_FACE",FACE,{"disambiguationData":[OSD([sQuery(id+"F2.wireOp",EDGE,"E4.3.15.0")])]})]});
            var Q318;
            Q318=makeQuery(id+"F3.boolean.opBoolean","COPY",EDGE,{"derivedFrom":makeQuery(id+"F3.opExtrude","SWEPT_EDGE",EDGE,{"disambiguationData":[OSD([sQuery(id+"F0.wireOp",EDGE,"E1"),sQuery(id+"F2.wireOp",EDGE,"E3.9.0.2")])]})});
            var Q319;
            Q319=makeQuery(id+"F3.boolean.opBoolean","COPY",EDGE,{"derivedFrom":makeQuery(id+"F3.opExtrude","SWEPT_EDGE",EDGE,{"disambiguationData":[OSD([sQuery(id+"F0.wireOp",EDGE,"E1"),sQuery(id+"F2.wireOp",EDGE,"E4.6.17.0")])]})});
            var Q320;
            Q320=makeQuery(id+"F3.boolean.opBoolean","COPY",EDGE,{"derivedFrom":makeQuery(id+"F3.opExtrude","CAP_EDGE",EDGE,{"disambiguationData":[OSD([sQuery(id+"F2.wireOp",EDGE,"E3.14.0.1")])],"isStart":true})});
            var Q321;
            Q321=makeQuery(id+"F3.boolean.opBoolean","INTERSECT",EDGE,{"derivedFrom":[makeQuery(id+"F1.opExtrude","CAP_FACE",FACE,{"disambiguationData":[OSD([sQuery(id+"F0.wireOp",EDGE,"E0"),sQuery(id+"F0.wireOp",EDGE,"E1")])],"isStart":true}),makeQuery(id+"F3.opExtrude","SWEPT_FACE",FACE,{"disambiguationData":[OSD([sQuery(id+"F2.wireOp",EDGE,"E3.10.0.1")])]})]});
            var Q322;
            Q322=makeQuery(id+"F3.boolean.opBoolean","COPY",EDGE,{"derivedFrom":makeQuery(id+"F3.opExtrude","SWEPT_EDGE",EDGE,{"disambiguationData":[OSD([sQuery(id+"F2.wireOp",EDGE,"E3.14.0.0"),sQuery(id+"F2.wireOp",EDGE,"E3.14.0.1")])]})});
            var Q323;
            Q323=makeQuery(id+"F3.boolean.opBoolean","COPY",EDGE,{"derivedFrom":makeQuery(id+"F3.opExtrude","SWEPT_EDGE",EDGE,{"disambiguationData":[OSD([sQuery(id+"F0.wireOp",EDGE,"E1"),sQuery(id+"F2.wireOp",EDGE,"E3.10.0.0")])]})});
            var Q324;
            Q324=makeQuery(id+"F3.boolean.opBoolean","COPY",EDGE,{"derivedFrom":makeQuery(id+"F3.opExtrude","SWEPT_EDGE",EDGE,{"disambiguationData":[OSD([sQuery(id+"F0.wireOp",EDGE,"E1"),sQuery(id+"F2.wireOp",EDGE,"E5.0.18.0")])]})});
            var Q325;
            Q325=makeQuery(id+"F3.boolean.opBoolean","COPY",EDGE,{"derivedFrom":makeQuery(id+"F3.opExtrude","CAP_EDGE",EDGE,{"disambiguationData":[OSD([sQuery(id+"F2.wireOp",EDGE,"E3.9.0.1")])],"isStart":true})});
            var Q326;
            Q326=makeQuery(id+"F3.boolean.opBoolean","INTERSECT",EDGE,{"derivedFrom":[makeQuery(id+"F1.opExtrude","CAP_FACE",FACE,{"disambiguationData":[OSD([sQuery(id+"F0.wireOp",EDGE,"E0"),sQuery(id+"F0.wireOp",EDGE,"E1")])],"isStart":true}),makeQuery(id+"F3.opExtrude","SWEPT_FACE",FACE,{"disambiguationData":[OSD([sQuery(id+"F2.wireOp",EDGE,"E2.bottom")])]})]});
            var Q327;
            Q327=makeQuery(id+"F3.boolean.opBoolean","INTERSECT",EDGE,{"derivedFrom":[makeQuery(id+"F1.opExtrude","CAP_FACE",FACE,{"disambiguationData":[OSD([sQuery(id+"F0.wireOp",EDGE,"E0"),sQuery(id+"F0.wireOp",EDGE,"E1")])],"isStart":true}),makeQuery(id+"F3.opExtrude","SWEPT_FACE",FACE,{"disambiguationData":[OSD([sQuery(id+"F2.wireOp",EDGE,"E3.5.0.1")])]})]});
            var Q328;
            Q328=makeQuery(id+"F3.boolean.opBoolean","COPY",EDGE,{"derivedFrom":makeQuery(id+"F3.opExtrude","CAP_EDGE",EDGE,{"disambiguationData":[OSD([sQuery(id+"F2.wireOp",EDGE,"E4.3.16.0")])],"isStart":true})});
            var Q329;
            Q329=makeQuery(id+"F3.boolean.opBoolean","COPY",EDGE,{"derivedFrom":makeQuery(id+"F3.opExtrude","CAP_EDGE",EDGE,{"disambiguationData":[OSD([sQuery(id+"F2.wireOp",EDGE,"E5.3.18.0")])],"isStart":true})});
            fillet(context, id + "F4", {"entities" : qUnion([Q0, Q1, Q2, Q3, Q4, Q5, Q6, Q7, Q8, Q9, Q10, Q11, Q12, Q13, Q14, Q15, Q16, Q17, Q18, Q19, Q20, Q21, Q22, Q23, Q24, Q25, Q26, Q27, Q28, Q29, Q30, Q31, Q32, Q33, Q34, Q35, Q36, Q37, Q38, Q39, Q40, Q41, Q42, Q43, Q44, Q45, Q46, Q47, Q48, Q49, Q50, Q51, Q52, Q53, Q54, Q55, Q56, Q57, Q58, Q59, Q60, Q61, Q62, Q63, Q64, Q65, Q66, Q67, Q68, Q69, Q70, Q71, Q72, Q73, Q74, Q75, Q76, Q77, Q78, Q79, Q80, Q81, Q82, Q83, Q84, Q85, Q86, Q87, Q88, Q89, Q90, Q91, Q92, Q93, Q94, Q95, Q96, Q97, Q98, Q99, Q100, Q101, Q102, Q103, Q104, Q105, Q106, Q107, Q108, Q109, Q110, Q111, Q112, Q113, Q114, Q115, Q116, Q117, Q118, Q119, Q120, Q121, Q122, Q123, Q124, Q125, Q126, Q127, Q128, Q129, Q130, Q131, Q132, Q133, Q134, Q135, Q136, Q137, Q138, Q139, Q140, Q141, Q142, Q143, Q144, Q145, Q146, Q147, Q148, Q149, Q150, Q151, Q152, Q153, Q154, Q155, Q156, Q157, Q158, Q159, Q160, Q161, Q162, Q163, Q164, Q165, Q166, Q167, Q168, Q169, Q170, Q171, Q172, Q173, Q174, Q175, Q176, Q177, Q178, Q179, Q180, Q181, Q182, Q183, Q184, Q185, Q186, Q187, Q188, Q189, Q190, Q191, Q192, Q193, Q194, Q195, Q196, Q197, Q198, Q199, Q200, Q201, Q202, Q203, Q204, Q205, Q206, Q207, Q208, Q209, Q210, Q211, Q212, Q213, Q214, Q215, Q216, Q217, Q218, Q219, Q220, Q221, Q222, Q223, Q224, Q225, Q226, Q227, Q228, Q229, Q230, Q231, Q232, Q233, Q234, Q235, Q236, Q237, Q238, Q239, Q240, Q241, Q242, Q243, Q244, Q245, Q246, Q247, Q248, Q249, Q250, Q251, Q252, Q253, Q254, Q255, Q256, Q257, Q258, Q259, Q260, Q261, Q262, Q263, Q264, Q265, Q266, Q267, Q268, Q269, Q270, Q271, Q272, Q273, Q274, Q275, Q276, Q277, Q278, Q279, Q280, Q281, Q282, Q283, Q284, Q285, Q286, Q287, Q288, Q289, Q290, Q291, Q292, Q293, Q294, Q295, Q296, Q297, Q298, Q299, Q300, Q301, Q302, Q303, Q304, Q305, Q306, Q307, Q308, Q309, Q310, Q311, Q312, Q313, Q314, Q315, Q316, Q317, Q318, Q319, Q320, Q321, Q322, Q323, Q324, Q325, Q326, Q327, Q328, Q329]), "radius" : 1 * mm, "tangentPropagation" : true, "allowEdgeOverflow" : false});
        }
        {
            var Q0;
            Q0=makeQuery(id+"F1.opExtrude","CAP_FACE",FACE,{"disambiguationData":[OSD([sQuery(id+"F0.wireOp",EDGE,"E0"),sQuery(id+"F0.wireOp",EDGE,"E1")])],"isStart":false});
            var sketch = newSketch(context, id + "F5", { "sketchPlane" : qUnion([Q0])});
            skCircle(sketch, "E7", {"center": v(-68.77, 53.37) * mm, "radius": 2.37 * mm});
            skSolve(sketch);
        }
        {
            var Q0;
            Q0=makeQuery(id+"F5.imprint","IMPRINT",FACE,{"disambiguationData":[TD([[makeQuery(id+"F5.imprint","IMPRINT",EDGE,{"derivedFrom":sQuery(id+"F5.wireOp",EDGE,"E7")}),1.0]])]});
            extrude(context, id + "F6", {"entities" : qUnion([Q0]), "operationType" : NewBodyOperationType.REMOVE, "oppositeDirection" : true, "depth" : 4 * mm});
        }
        {
            var Q0;
            Q0=makeQuery(id+"F6.boolean.opBoolean","COPY",FACE,{"derivedFrom":makeQuery(id+"F6.opExtrude","SWEPT_FACE",FACE,{"disambiguationData":[OSD([sQuery(id+"F5.wireOp",EDGE,"E7")])]})});
            var Q1;
            Q1=makeQuery(id+"F6.boolean.opBoolean","COPY",EDGE,{"derivedFrom":makeQuery(id+"F6.opExtrude","CAP_EDGE",EDGE,{"disambiguationData":[OSD([sQuery(id+"F5.wireOp",EDGE,"E7")])],"isStart":true})});
            var Q2;
            Q2=makeQuery(id+"F6.boolean.opBoolean","INTERSECT",EDGE,{"derivedFrom":[makeQuery(id+"F1.opExtrude","CAP_FACE",FACE,{"disambiguationData":[OSD([sQuery(id+"F0.wireOp",EDGE,"E0"),sQuery(id+"F0.wireOp",EDGE,"E1")])],"isStart":true}),makeQuery(id+"F6.opExtrude","SWEPT_FACE",FACE,{"disambiguationData":[OSD([sQuery(id+"F5.wireOp",EDGE,"E7")])]})]});
            fillet(context, id + "F7", {"entities" : qUnion([Q0, Q1, Q2]), "radius" : 1 * mm, "tangentPropagation" : true, "allowEdgeOverflow" : false});
        }
        {
            var Q0;
            Q0=makeQuery(id+"F1.opExtrude","CAP_FACE",FACE,{"disambiguationData":[OSD([sQuery(id+"F0.wireOp",EDGE,"E0"),sQuery(id+"F0.wireOp",EDGE,"E1")])],"isStart":false});
            var sketch = newSketch(context, id + "F8", { "sketchPlane" : qUnion([Q0])});
            skText(sketch, "E8", { "text": "Netterlee", "fontName": "OpenSans-Regular.ttf"});
            const initialGuessF8  = {"E8": [-0.06124, 0.0572, 1, 0, 0.00905]};
            skSetInitialGuess(sketch, initialGuessF8);
            skSolve(sketch);
        }
        {
            var Q0;
            Q0 = qSketchRegion(id + "F8", true);
            extrude(context, id + "F9", {"entities" : qUnion([Q0]), "operationType" : NewBodyOperationType.REMOVE, "oppositeDirection" : true, "depth" : 37.2 * mm});
        }
    });
